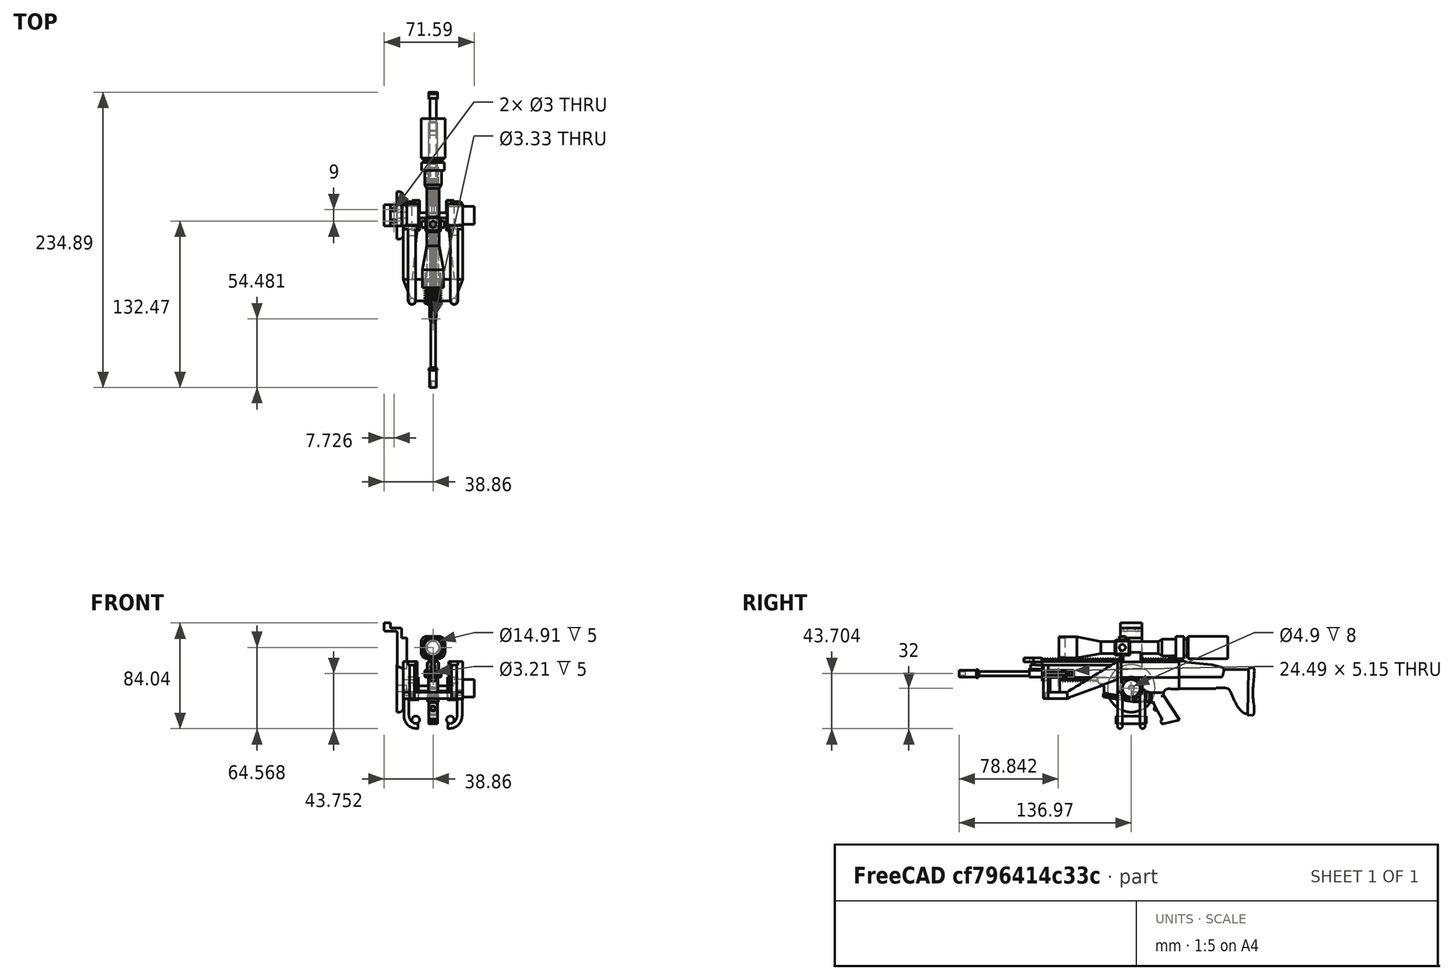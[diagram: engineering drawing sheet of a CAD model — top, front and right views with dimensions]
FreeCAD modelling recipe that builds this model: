
FCSTD DOCUMENT  (FreeCAD 1.0R39319 (Git))
Label: turretShooter
License: All rights reserved
LicenseURL: https://en.wikipedia.org/wiki/All_rights_reserved
objects: Sketcher::SketchObject×58, PartDesign::Pad×29, PartDesign::Pocket×14, PartDesign::Plane×10, PartDesign::Mirrored×8, Image::ImagePlane×4, PartDesign::Fillet×4, PartDesign::LinearPattern×3, PartDesign::Revolution×3, PartDesign::Chamfer×2, PartDesign::AdditiveLoft×1, PartDesign::AdditivePipe×1, PartDesign::MultiTransform×1, Part::Part2DObjectPython×1, PartDesign::Body×1
note: 314 computed .brp shape members not serialized (recipe doc carries the construction recipe); baked Part::Feature solids carry a one-line shape summary decoded from their .brp

FEATURE [Image::ImagePlane] The_Finals_Screenshot_2026  label="The Finals Screenshot 2026"
  Placement = pos=(0,0,0) rot=(0.57735,0.57735,0.57735;2.0944rad)
  XSize = 826.63
  YSize = 464.98
FEATURE [Image::ImagePlane] The_Finals_Screenshot_2025  label="The Finals Screenshot 2025"
  Placement = pos=(0,0,0) rot=(1,0,0;1.5708rad)
  XSize = 826.629
  YSize = 464.979
FEATURE [Image::ImagePlane] T______H___E____________F____________I_______________N______AL_________S_10_02_2025_2_09_09_pm  label="T​﻿H​E ​​​F​﻿﻿​I​﻿​﻿​N​​AL​​​S 10_02_2025 2_09_09 pm"
  Placement = pos=(0,2,83) rot=(0.57735,0.57735,0.57735;2.0944rad)
  XSize = 260.56
  YSize = 146.56
FEATURE [Image::ImagePlane] T______H___E____________F____________I_______________N______AL_________S_10_02_2025_2_07_41_pm  label="T​﻿H​E ​​​F​﻿﻿​I​﻿​﻿​N​​AL​​​S 10_02_2025 2_07_41 pm"
  Placement = pos=(0,0,92) rot=(1,0,0;1.5708rad)
  XSize = 193.32
  YSize = 108.74
FEATURE [Sketcher::SketchObject] Sketch
  ArcFitTolerance = 1e-06
  AttachmentSupport = -> [YZ_Plane]
  FullyConstrained = true
  MakeInternals = false
  MapMode = 5
  Placement = pos=(0,0,0) rot=(0.57735,0.57735,0.57735;2.0944rad)
  sketch-geometry (1):
    g0: LineSegment StartX=-70.97 StartY=87.59 StartZ=0 EndX=38.21 EndY=87.59 EndZ=0
  constraints (4):
    c: Horizontal(g0)
    c: Distance(g-1,g0) = 87.59
    c: DistanceX(g0,g0) = 109.18
    c: Distance(g0,g-2) = 70.97
FEATURE [PartDesign::Plane] DatumPlane
  AttachmentSupport = -> [Sketch,XZ_Plane]
  Length = 178.251
  MapMode = 6
  Placement = pos=(0,-70.97,87.59) rot=(0.57735,-0.57735,0.57735;2.0944rad)
  ResizeMode = 0
  Width = 92.8021
FEATURE [Sketcher::SketchObject] Sketch001
  ArcFitTolerance = 1e-06
  AttachmentSupport = -> [DatumPlane]
  FullyConstrained = true
  MakeInternals = false
  MapMode = 5
  Placement = pos=(0,-70.97,87.59) rot=(0.57735,-0.57735,0.57735;2.0944rad)
  sketch-geometry (14):
    g0: LineSegment StartX=1.18 StartY=-4.62 StartZ=0 EndX=12.07 EndY=-4.62 EndZ=0
    g1: LineSegment StartX=13.56 StartY=-3.13 StartZ=0 EndX=13.56 EndY=-2.51 EndZ=0
    g2: LineSegment StartX=13.56 StartY=-2.51 StartZ=0 EndX=15.93 EndY=-2.51 EndZ=0
    g3: LineSegment StartX=15.93 StartY=-2.51 StartZ=0 EndX=15.93 EndY=2.51 EndZ=0
    g4: LineSegment StartX=15.93 StartY=2.51 StartZ=0 EndX=13.56 EndY=2.51 EndZ=0
    g5: LineSegment StartX=13.56 StartY=2.51 StartZ=0 EndX=13.56 EndY=3.13 EndZ=0
    g6: LineSegment StartX=12.07 StartY=4.62 StartZ=0 EndX=1.18 EndY=4.62 EndZ=0
    g7: LineSegment [constr] StartX=7.37 StartY=4.62 StartZ=0 EndX=7.37 EndY=0 EndZ=0
    g8: LineSegment [constr] StartX=7.37 StartY=0 StartZ=0 EndX=7.37 EndY=-4.62 EndZ=0
    g9: LineSegment StartX=1.18 StartY=4.62 StartZ=0 EndX=1.18 EndY=-4.62 EndZ=0
    g10: ArcOfCircle CenterX=12.07 CenterY=3.13 CenterZ=0 NormalX=0 NormalY=0 NormalZ=1 AngleXU=0 Radius=1.49 StartAngle=0 EndAngle=1.5708
    g11: GeomPoint [constr] X=13.56 Y=4.62 Z=0
    g12: ArcOfCircle CenterX=12.07 CenterY=-3.13 CenterZ=0 NormalX=0 NormalY=0 NormalZ=1 AngleXU=0 Radius=1.49 StartAngle=4.71239 EndAngle=6.28319
    g13: GeomPoint [constr] X=13.56 Y=-4.62 Z=0
  constraints (38):
    c: Horizontal(g0)
    c: Vertical(g1)
    c: Coincident(g1,g2)
    c: Horizontal(g2)
    c: Coincident(g2,g3)
    c: Vertical(g3)
    c: Coincident(g3,g4)
    c: Horizontal(g4)
    c: Coincident(g4,g5)
    c: Vertical(g5)
    c: Horizontal(g6)
    c: Symmetric(g11,g6,g7)
    c: PointOnObject(g7,g-1)
    c: Vertical(g7)
    c: Coincident(g8,g7)
    c: PointOnObject(g8,g0)
    c: Vertical(g8)
    c: Equal(g8,g7)
    c: Coincident(g9,g6)
    c: Coincident(g9,g0)
    c: Vertical(g9)
    c: DistanceY(g9,g9) = 9.24
    c: DistanceX(g6,g11) = 12.38
    c: DistanceY(g3,g3) = 5.02
    c: Distance(g-1,g9) = 1.18
    c: DistanceX(g4,g4) = 2.37
    c: PointOnObject(g11,g5)
    c: PointOnObject(g11,g6)
    c: Tangent(g5,g10) = -1.5708
    c: Tangent(g6,g10) = -1.5708
    c: PointOnObject(g13,g0)
    c: PointOnObject(g13,g1)
    c: Tangent(g0,g12) = -1.5708
    c: Tangent(g1,g12) = -1.5708
    c: Equal(g12,g10)
    c: Radius(g10) = 1.49
    c: Equal(g0,g6)
    c: Equal(g1,g5)
FEATURE [PartDesign::Pad] Pad
  Direction = (0,-1,0)
  Length = 109
  Length2 = 10
  Placement = pos=(0,-70.97,87.59) rot=(0.57735,-0.57735,0.57735;2.0944rad)
  Profile = -> Sketch001
  ReferenceAxis = -> Sketch001 [N_Axis]
  Refine = true
  Reversed = true
  Suppressed = false
  Type = 0
  UpToShape = -> [Sketch]
FEATURE [Sketcher::SketchObject] Sketch002
  ArcFitTolerance = 1e-06
  AttachmentSupport = -> [YZ_Plane]
  FullyConstrained = true
  MakeInternals = false
  MapMode = 5
  Placement = pos=(0,0,0) rot=(0.57735,0.57735,0.57735;2.0944rad)
FEATURE [Sketcher::SketchObject] Sketch003
  ArcFitTolerance = 1e-06
  AttachmentSupport = -> [YZ_Plane]
  ExternalGeometry = -> [Pad]
  FullyConstrained = false
  MakeInternals = false
  MapMode = 5
  Placement = pos=(0,0,0) rot=(0.57735,0.57735,0.57735;2.0944rad)
  sketch-geometry (29):
    g0-g3: GeomPoint [constr] x4 (B-spline internal-alignment scaffolding for g4; pole/knot coordinates omitted)
    g4: BSplineCurve PolesCount=6 KnotsCount=4 Degree=3 IsPeriodic=0
    g5-g10: Circle [constr] x6 (B-spline internal-alignment scaffolding for g4; pole/knot coordinates omitted)
    g11: LineSegment StartX=-21.7658 StartY=81.0348 StartZ=0 EndX=-21.5863 EndY=76.1617 EndZ=0
    g12: LineSegment StartX=-21.5863 StartY=76.1617 StartZ=0 EndX=-22.4223 EndY=74.4999 EndZ=0
    g13: LineSegment StartX=-22.4223 StartY=74.4999 StartZ=0 EndX=-22.4223 EndY=73.2638 EndZ=0
    g14: LineSegment StartX=-22.4223 StartY=73.2638 StartZ=0 EndX=1.29753 EndY=69.2316 EndZ=0
    g15: LineSegment StartX=1.29753 StartY=69.2316 StartZ=0 EndX=1.29753 EndY=77.3277 EndZ=0
    g16: LineSegment StartX=1.29753 StartY=77.3277 StartZ=0 EndX=13.9295 EndY=77.3277 EndZ=0
    g17: LineSegment StartX=13.9295 StartY=77.3277 StartZ=0 EndX=14.8282 EndY=76.5716 EndZ=0
    g18: LineSegment StartX=14.8282 StartY=76.5716 StartZ=0 EndX=25.6744 EndY=76.5716 EndZ=0
    g19: GeomPoint [constr] X=25.6744 Y=76.5716 Z=0
    g20: GeomPoint [constr] X=27.7174 Y=79.2735 Z=0
    g21: GeomPoint [constr] X=33.2888 Y=79.6145 Z=0
    g22: BSplineCurve PolesCount=4 KnotsCount=2 Degree=3 IsPeriodic=0
    g23-g26: Circle [constr] x4 (B-spline internal-alignment scaffolding for g22; pole/knot coordinates omitted)
    g27: LineSegment StartX=33.2888 StartY=79.6145 StartZ=0 EndX=33.2888 EndY=88.77 EndZ=0
    g28: LineSegment StartX=33.2888 StartY=88.77 StartZ=0 EndX=-26.675 EndY=88.77 EndZ=0
  constraints (43):
    c: InternalAlignment(g0-g3 -> g4) x4
    c: InternalAlignment(g5,g4)
    c: Weight(g5) = 1
    c: InternalAlignment(g6,g4)
    c: Equal(g6,g5)
    c: InternalAlignment(g7,g4)
    c: Equal(g7,g5)
    c: InternalAlignment(g8,g4)
    c: Equal(g8,g5)
    c: InternalAlignment(g9,g4)
    c: Equal(g9,g5)
    c: InternalAlignment(g10,g4)
    c: Equal(g10,g5)
    c: PointOnObject(g0,g-3)
    c: Coincident(g11,g4)
    c: Coincident(g11,g12)
    c: Coincident(g12,g13)
    c: Vertical(g13)
    c: Coincident(g13,g14)
    c: Coincident(g14,g15)
    c: Vertical(g15)
    c: Coincident(g15,g16)
    c: Horizontal(g16)
    c: Coincident(g16,g17)
    c: Coincident(g17,g18)
    c: Horizontal(g18)
    c: InternalAlignment(g19,g22)
    c: PointOnObject(g20,g22)
    c: InternalAlignment(g21,g22)
    c: InternalAlignment(g23,g22)
    c: Weight(g23) = 1
    c: InternalAlignment(g24,g22)
    c: Equal(g24,g23)
    c: InternalAlignment(g25,g22)
    c: Equal(g25,g23)
    c: InternalAlignment(g26,g22)
    c: Equal(g26,g23)
    c: Coincident(g19,g18)
    c: Coincident(g27,g22)
    c: PointOnObject(g27,g-3)
    c: Vertical(g27)
    c: Coincident(g27,g28)
    c: Coincident(g28,g4)
FEATURE [PartDesign::Pad] Pad001
  BaseFeature = -> Pad
  Direction = (1,0,0)
  Length = 10
  Length2 = 10
  Midplane = true
  Offset = 1
  Placement = pos=(0,-70.97,87.59) rot=(0.57735,-0.57735,0.57735;2.0944rad)
  Profile = -> Sketch003
  ReferenceAxis = -> Sketch003 [N_Axis]
  Refine = true
  Suppressed = false
  Type = 3
  UpToFace = -> Pad [Face1]
FEATURE [PartDesign::Mirrored] Mirrored
  BaseFeature = -> Pad001
  MirrorPlane = -> YZ_Plane
  Originals = -> [Pad001]
  Placement = pos=(0,-70.97,87.59) rot=(0.57735,-0.57735,0.57735;2.0944rad)
  Refine = true
  Suppressed = false
  TransformMode = 0
FEATURE [Sketcher::SketchObject] Sketch004
  ArcFitTolerance = 1e-06
  AttachmentSupport = -> [YZ_Plane]
  ExternalGeometry = -> [Mirrored]
  FullyConstrained = false
  MakeInternals = false
  MapMode = 5
  Placement = pos=(0,0,0) rot=(0.57735,0.57735,0.57735;2.0944rad)
  sketch-geometry (17):
    g0: LineSegment StartX=16.9081 StartY=76.5716 StartZ=0 EndX=16.5743 EndY=76.3186 EndZ=0
    g1: LineSegment StartX=16.5743 StartY=76.3186 StartZ=0 EndX=16.2831 EndY=75.8195 EndZ=0
    g2: LineSegment StartX=16.2831 StartY=75.8195 StartZ=0 EndX=16.2831 EndY=68.7742 EndZ=0
    g3: LineSegment StartX=16.2831 StartY=68.7742 StartZ=0 EndX=17.4672 EndY=68.726 EndZ=0
    g4: LineSegment StartX=17.4672 StartY=68.726 StartZ=0 EndX=19.0481 EndY=65.7646 EndZ=0
    g5: LineSegment StartX=19.0481 StartY=65.7646 StartZ=0 EndX=18.1135 EndY=63.3561 EndZ=0
    g6: LineSegment StartX=18.1135 StartY=63.3561 StartZ=0 EndX=18.473 EndY=62.6731 EndZ=0
    g7: LineSegment StartX=18.473 StartY=62.6731 StartZ=0 EndX=19.6952 EndY=62.5293 EndZ=0
    g8: LineSegment StartX=19.6952 StartY=62.5293 StartZ=0 EndX=21.0612 EndY=61.9181 EndZ=0
    g9: LineSegment StartX=21.0612 StartY=61.9181 StartZ=0 EndX=24.3711 EndY=55.6421 EndZ=0
    g10: LineSegment StartX=24.3711 StartY=55.6421 StartZ=0 EndX=23.5443 EndY=53.665 EndZ=0
    g11: LineSegment StartX=23.5443 StartY=53.665 StartZ=0 EndX=24.5508 EndY=51.7957 EndZ=0
    g12: LineSegment StartX=24.5508 StartY=51.7957 StartZ=0 EndX=37.0608 EndY=54.4199 EndZ=0
    g13: LineSegment StartX=37.0608 StartY=54.4199 StartZ=0 EndX=38.3549 EndY=55.1388 EndZ=0
    g14: LineSegment StartX=38.3549 StartY=55.1388 StartZ=0 EndX=25.6744 EndY=74.3298 EndZ=0
    g15: LineSegment StartX=25.6744 StartY=74.3298 StartZ=0 EndX=25.6744 EndY=76.5716 EndZ=0
    g16: LineSegment StartX=16.9081 StartY=76.5716 StartZ=0 EndX=25.6744 EndY=76.5716 EndZ=0
  constraints (21):
    c: PointOnObject(g0,g-3)
    c: Coincident(g0,g1)
    c: Coincident(g1,g2)
    c: Vertical(g2)
    c: Coincident(g2,g3)
    c: Coincident(g3,g4)
    c: Coincident(g4,g5)
    c: Coincident(g5,g6)
    c: Coincident(g6,g7)
    c: Coincident(g7,g8)
    c: Coincident(g8,g9)
    c: Coincident(g9,g10)
    c: Coincident(g10,g11)
    c: Coincident(g11,g12)
    c: Coincident(g12,g13)
    c: Coincident(g13,g14)
    c: Coincident(g14,g15)
    c: Coincident(g15,g-3)
    c: Vertical(g15)
    c: Coincident(g16,g0)
    c: Coincident(g16,g15)
FEATURE [PartDesign::Pad] Pad002
  BaseFeature = -> Mirrored
  Direction = (1,0,0)
  Length = 7
  Length2 = 10
  Midplane = true
  Placement = pos=(0,-70.97,87.59) rot=(0.57735,-0.57735,0.57735;2.0944rad)
  Profile = -> Sketch004
  ReferenceAxis = -> Sketch004 [N_Axis]
  Refine = true
  Suppressed = false
  Type = 0
FEATURE [Sketcher::SketchObject] Sketch005
  ArcFitTolerance = 1e-06
  AttachmentSupport = -> [Pad002]
  ExternalGeometry = -> [Pad002]
  FullyConstrained = false
  MakeInternals = false
  MapMode = 5
  Placement = pos=(3.5,-70.97,87.59) rot=(0.707107,0,0.707107;3.14159rad)
  sketch-geometry (4):
    g0: LineSegment StartX=-25.6719 StartY=-92.0312 StartZ=0 EndX=-21.8254 EndY=-90.0181 EndZ=0
    g1: LineSegment StartX=-25.6719 StartY=-92.0312 StartZ=0 EndX=-26.772 EndY=-88.7379 EndZ=0
    g2: LineSegment StartX=-26.772 StartY=-88.7379 StartZ=0 EndX=-23.2386 EndY=-88.3381 EndZ=0
    g3: LineSegment StartX=-23.2386 StartY=-88.3381 StartZ=0 EndX=-21.8254 EndY=-90.0181 EndZ=0
  constraints (6):
    c: Coincident(g-9,g0)
    c: Coincident(g0,g-4)
    c: Coincident(g0,g1)
    c: Coincident(g1,g2)
    c: Coincident(g2,g3)
    c: Coincident(g3,g0)
FEATURE [PartDesign::Pocket] Pocket
  BaseFeature = -> Pad002
  Direction = (-1,0,2e-16)
  Length = 2
  Length2 = 5
  Placement = pos=(0,-70.97,87.59) rot=(0.57735,-0.57735,0.57735;2.0944rad)
  Profile = -> Sketch005
  ReferenceAxis = -> Sketch005 [N_Axis]
  Refine = true
  Suppressed = false
  Type = 0
FEATURE [PartDesign::Mirrored] Mirrored001
  BaseFeature = -> Pocket
  MirrorPlane = -> YZ_Plane
  Originals = -> [Pocket]
  Placement = pos=(0,-70.97,87.59) rot=(0.57735,-0.57735,0.57735;2.0944rad)
  Refine = true
  Suppressed = false
  TransformMode = 0
FEATURE [PartDesign::Fillet] Fillet
  Base = -> Mirrored001 [Edge88,Edge87,Edge86,Edge85,Edge84,Edge100,Edge101,Edge102,Edge99,Edge98]
  BaseFeature = -> Mirrored001
  Placement = pos=(0,-70.97,87.59) rot=(0.57735,-0.57735,0.57735;2.0944rad)
  Radius = 1
  Refine = true
  SupportTransform = false
  Suppressed = false
  UseAllEdges = false
FEATURE [PartDesign::Fillet] Fillet001
  Base = -> Fillet [Edge5,Edge7,Edge28,Edge33]
  BaseFeature = -> Fillet
  Placement = pos=(0,-70.97,87.59) rot=(0.57735,-0.57735,0.57735;2.0944rad)
  Radius = 2
  Refine = true
  SupportTransform = false
  Suppressed = false
  UseAllEdges = false
FEATURE [PartDesign::Fillet] Fillet002
  Base = -> Fillet001 [Edge139,Edge162,Edge136,Edge161]
  BaseFeature = -> Fillet001
  Placement = pos=(0,-70.97,87.59) rot=(0.57735,-0.57735,0.57735;2.0944rad)
  Radius = 0.5
  Refine = true
  SupportTransform = false
  Suppressed = false
  UseAllEdges = false
FEATURE [PartDesign::Pad] Pad003
  BaseFeature = -> Fillet002
  Direction = (1e-16,1,0)
  Length = 10
  Length2 = 10
  Placement = pos=(0,-70.97,87.59) rot=(0.57735,-0.57735,0.57735;2.0944rad)
  Profile = -> Fillet002 [Face47]
  Refine = true
  Suppressed = false
  Type = 3
  UpToFace = -> Fillet002 [Face59]
FEATURE [Sketcher::SketchObject] Sketch006
  ArcFitTolerance = 1e-06
  AttachmentSupport = -> [YZ_Plane]
  ExternalGeometry = -> [Pad003]
  FullyConstrained = false
  MakeInternals = false
  MapMode = 5
  Placement = pos=(0,0,0) rot=(0.57735,0.57735,0.57735;2.0944rad)
  sketch-geometry (35):
    g0: LineSegment StartX=1.64111 StartY=70.8438 StartZ=0 EndX=2.72621 EndY=70.1138 EndZ=0
    g1: LineSegment StartX=2.72621 StartY=70.1138 StartZ=0 EndX=13.0839 EndY=69.8573 EndZ=0
    g2: LineSegment StartX=13.0839 StartY=69.8573 StartZ=0 EndX=13.6758 EndY=70.1533 EndZ=0
    g3: LineSegment StartX=13.6758 StartY=70.1533 StartZ=0 EndX=14.2084 EndY=70.5873 EndZ=0
    g4: LineSegment StartX=14.2084 StartY=70.5873 StartZ=0 EndX=14.5241 EndY=71.1397 EndZ=0
    g5: LineSegment StartX=14.5241 StartY=71.1397 StartZ=0 EndX=14.5241 EndY=76.8274 EndZ=0
    g6: LineSegment StartX=14.5241 StartY=76.8274 StartZ=0 EndX=13.9295 EndY=77.3277 EndZ=0
    g7: LineSegment StartX=2.3119 StartY=77.3277 StartZ=0 EndX=1.8384 EndY=76.9203 EndZ=0
    g8: LineSegment StartX=1.8384 StartY=76.9203 StartZ=0 EndX=1.64111 EndY=76.6441 EndZ=0
    g9: LineSegment StartX=1.64111 StartY=76.6441 StartZ=0 EndX=1.64111 EndY=70.8438 EndZ=0
    g10: LineSegment StartX=1.29754 StartY=69.2316 StartZ=0 EndX=16.2831 EndY=69.2316 EndZ=0
    g11: LineSegment StartX=16.2831 StartY=69.2316 StartZ=0 EndX=18.1597 EndY=78.374 EndZ=0
    g12: LineSegment StartX=18.1597 StartY=78.374 StartZ=0 EndX=0.618146 EndY=78.374 EndZ=0
    g13: LineSegment StartX=0.618146 StartY=78.374 StartZ=0 EndX=1.29754 EndY=69.2316 EndZ=0
    g14: LineSegment StartX=13.9295 StartY=77.3277 StartZ=0 EndX=11.92 EndY=77.3277 EndZ=0
    g15: LineSegment StartX=11.92 StartY=77.3277 StartZ=0 EndX=11.92 EndY=72.0294 EndZ=0
    g16-g19: Circle [constr] x4 (B-spline internal-alignment scaffolding for g20; pole/knot coordinates omitted)
    g20: BSplineCurve PolesCount=4 KnotsCount=2 Degree=3 IsPeriodic=0
    g21: GeomPoint [constr] X=11.92 Y=72.0294 Z=0
    g22: GeomPoint [constr] X=9.76933 Y=70.1931 Z=0
    g23-g26: GeomPoint [constr] x4 (B-spline internal-alignment scaffolding for g27; pole/knot coordinates omitted)
    g27: BSplineCurve PolesCount=6 KnotsCount=4 Degree=3 IsPeriodic=0
    g28-g33: Circle [constr] x6 (B-spline internal-alignment scaffolding for g27; pole/knot coordinates omitted)
    g34: LineSegment StartX=7.6135 StartY=77.3277 StartZ=0 EndX=2.3119 EndY=77.3277 EndZ=0
  constraints (52):
    c: Coincident(g0,g1)
    c: Coincident(g1,g2)
    c: Coincident(g2,g3)
    c: Coincident(g3,g4)
    c: Coincident(g4,g5)
    c: PointOnObject(g5,g-6)
    c: Vertical(g5)
    c: Coincident(g5,g6)
    c: Coincident(g6,g-6)
    c: PointOnObject(g7,g-4)
    c: Coincident(g7,g8)
    c: Coincident(g8,g9)
    c: Vertical(g9)
    c: Coincident(g0,g9)
    c: Coincident(g-3,g10)
    c: PointOnObject(g10,g-7)
    c: Horizontal(g10)
    c: Coincident(g10,g11)
    c: Coincident(g11,g12)
    c: Horizontal(g12)
    c: Coincident(g12,g13)
    c: Coincident(g13,g10)
    c: Coincident(g6,g14)
    c: PointOnObject(g14,g-4)
    c: Coincident(g14,g15)
    c: Vertical(g15)
    c: Weight(g16) = 1
    c: Equal(g16,g17)
    c: Equal(g16,g18)
    c: Equal(g16,g19)
    c: InternalAlignment(g16-g19 -> g20) x4
    c: InternalAlignment(g21,g20)
    c: InternalAlignment(g22,g20)
    c: Coincident(g16,g15)
    c: PointOnObject(g19,g17)
    c: InternalAlignment(g23-g26 -> g27) x4
    c: InternalAlignment(g28,g27)
    c: Weight(g28) = 1
    c: InternalAlignment(g29,g27)
    c: Equal(g29,g28)
    c: InternalAlignment(g30,g27)
    c: Equal(g30,g28)
    c: InternalAlignment(g31,g27)
    c: Equal(g31,g28)
    c: InternalAlignment(g32,g27)
    c: Equal(g32,g28)
    c: InternalAlignment(g33,g27)
    c: Equal(g33,g28)
    c: Coincident(g23,g20)
    c: Symmetric(g-4,g-4,g26)
    c: Coincident(g34,g27)
    c: Coincident(g34,g7)
FEATURE [PartDesign::Pad] Pad004
  BaseFeature = -> Pad003
  Direction = (1,0,0)
  Length = 2
  Length2 = 10
  Midplane = true
  Placement = pos=(0,-70.97,87.59) rot=(0.57735,-0.57735,0.57735;2.0944rad)
  Profile = -> Sketch006
  ReferenceAxis = -> Sketch006 [N_Axis]
  Refine = true
  Suppressed = false
  Type = 0
FEATURE [Sketcher::SketchObject] Sketch008
  ArcFitTolerance = 1e-06
  AttachmentSupport = -> [Pad004]
  FullyConstrained = false
  MakeInternals = false
  MapMode = 5
  Placement = pos=(0,-70.97,87.59) rot=(0.57735,-0.57735,0.57735;2.0944rad)
  sketch-geometry (1):
    g0: Circle CenterX=4.16197 CenterY=0 CenterZ=0 NormalX=0 NormalY=0 NormalZ=1 AngleXU=0 Radius=2.67231
  constraints (1):
    c: PointOnObject(g0,g-1)
FEATURE [PartDesign::Pad] Pad006
  BaseFeature = -> Pad004
  Direction = (0,-1,0)
  Length = 10
  Length2 = 10
  Placement = pos=(0,-70.97,87.59) rot=(0.57735,-0.57735,0.57735;2.0944rad)
  Profile = -> Sketch008
  ReferenceAxis = -> Sketch008 [N_Axis]
  Refine = true
  Suppressed = false
  Type = 0
FEATURE [Sketcher::SketchObject] Sketch009
  ArcFitTolerance = 1e-06
  AttachmentSupport = -> [Pad006]
  ExternalGeometry = -> [Pad006]
  FullyConstrained = false
  MakeInternals = false
  MapMode = 5
  Placement = pos=(0,-80.97,87.59) rot=(0.57735,-0.57735,0.57735;2.0944rad)
  sketch-geometry (1):
    g0: Circle CenterX=4.16197 CenterY=0 CenterZ=0 NormalX=0 NormalY=0 NormalZ=1 AngleXU=0 Radius=1.8522
  constraints (1):
    c: Coincident(g0,g-3)
FEATURE [PartDesign::Pad] Pad007
  BaseFeature = -> Pad006
  Direction = (0,-1,0)
  Length = 40
  Length2 = 10
  Placement = pos=(0,-70.97,87.59) rot=(0.57735,-0.57735,0.57735;2.0944rad)
  Profile = -> Sketch009
  ReferenceAxis = -> Sketch009 [N_Axis]
  Refine = true
  Suppressed = false
  Type = 0
FEATURE [Sketcher::SketchObject] Sketch010
  ArcFitTolerance = 1e-06
  AttachmentSupport = -> [Pad007]
  ExternalGeometry = -> [Pad007]
  FullyConstrained = false
  MakeInternals = false
  MapMode = 5
  Placement = pos=(0,1.29753,87.59) rot=(0.57735,0.57735,0.57735;4.18879rad)
  sketch-geometry (4):
    g0: LineSegment StartX=-15.2831 StartY=3.62 StartZ=0 EndX=-16.9708 EndY=4.36603 EndZ=0
    g1: LineSegment StartX=-16.9708 StartY=4.36603 StartZ=0 EndX=-18.3584 EndY=4.36603 EndZ=0
    g2: LineSegment StartX=-18.3584 StartY=4.36603 StartZ=0 EndX=-18.3584 EndY=3.62 EndZ=0
    g3: LineSegment StartX=-18.3584 StartY=3.62 StartZ=0 EndX=-15.2831 EndY=3.62 EndZ=0
  constraints (8):
    c: Coincident(g0,g1)
    c: Horizontal(g1)
    c: Coincident(g1,g2)
    c: Coincident(g2,g-4)
    c: Coincident(g2,g3)
    c: Coincident(g3,g0)
    c: Vertical(g2)
    c: PointOnObject(g0,g-4)
FEATURE [PartDesign::Pad] Pad008
  BaseFeature = -> Pad007
  Direction = (-7e-16,0.985857,-0.167587)
  Length = 25
  Length2 = 10
  Placement = pos=(0,-70.97,87.59) rot=(0.57735,-0.57735,0.57735;2.0944rad)
  Profile = -> Sketch010
  ReferenceAxis = -> Pad007 [Edge158]
  Refine = true
  Reversed = true
  Suppressed = false
  Type = 3
  UpToFace = -> Pad007 [Face69]
FEATURE [PartDesign::Pocket] Pocket001
  BaseFeature = -> Pad008
  Direction = (1,0,-6.3e-15)
  Length = 5
  Length2 = 5
  Placement = pos=(0,-70.97,87.59) rot=(0.57735,-0.57735,0.57735;2.0944rad)
  Profile = -> Pad008 [Face87]
  Refine = true
  Suppressed = false
  Type = 0
FEATURE [Sketcher::SketchObject] Sketch011
  ArcFitTolerance = 1e-06
  AttachmentSupport = -> [Pocket001]
  ExternalGeometry = -> [Pocket001]
  FullyConstrained = false
  MakeInternals = false
  MapMode = 5
  Placement = pos=(3.62,-70.97,87.59) rot=(0.707107,0,0.707107;3.14159rad)
  sketch-geometry (4):
    g0: LineSegment StartX=-18.3584 StartY=-72.2675 StartZ=0 EndX=-18.3584 EndY=-73.1783 EndZ=0
    g1: LineSegment StartX=-18.3584 StartY=-73.1783 StartZ=0 EndX=-16.9935 EndY=-73.1783 EndZ=0
    g2: LineSegment StartX=-16.9935 StartY=-73.1783 StartZ=0 EndX=-15.2831 EndY=-72.2675 EndZ=0
    g3: LineSegment StartX=-15.2831 StartY=-72.2675 StartZ=0 EndX=-18.3584 EndY=-72.2675 EndZ=0
  constraints (8):
    c: Coincident(g-4,g0)
    c: Vertical(g0)
    c: Coincident(g0,g1)
    c: Horizontal(g1)
    c: Coincident(g1,g2)
    c: Coincident(g2,g-5)
    c: Coincident(g2,g3)
    c: Coincident(g3,g0)
FEATURE [PartDesign::Pad] Pad009
  BaseFeature = -> Pocket001
  Direction = (1,1.3e-15,1.8e-15)
  Length = 4
  Length2 = 3
  Placement = pos=(0,-70.97,87.59) rot=(0.57735,-0.57735,0.57735;2.0944rad)
  Profile = -> Sketch011
  ReferenceAxis = -> Sketch011 [N_Axis]
  Refine = true
  Reversed = true
  Suppressed = false
  Type = 4
FEATURE [PartDesign::Pocket] Pocket002
  BaseFeature = -> Pad009
  Direction = (-1.7e-15,1,2e-16)
  Length = 5
  Length2 = 5
  Placement = pos=(0,-70.97,87.59) rot=(0.57735,-0.57735,0.57735;2.0944rad)
  Profile = -> Pad009 [Face94]
  Refine = true
  Suppressed = false
  Type = 0
FEATURE [PartDesign::Mirrored] Mirrored002
  BaseFeature = -> Pocket002
  MirrorPlane = -> YZ_Plane
  Originals = -> [Pad008,Pocket001,Pad009,Pocket002]
  Placement = pos=(0,-70.97,87.59) rot=(0.57735,-0.57735,0.57735;2.0944rad)
  Refine = true
  Suppressed = false
  TransformMode = 0
FEATURE [Sketcher::SketchObject] Sketch012
  ArcFitTolerance = 1e-06
  AttachmentSupport = -> [Mirrored002]
  FullyConstrained = false
  MakeInternals = false
  MapMode = 5
  Placement = pos=(0,-70.97,87.59) rot=(0.57735,-0.57735,0.57735;2.0944rad)
  sketch-geometry (1):
    g0: Circle CenterX=9.39539 CenterY=0 CenterZ=0 NormalX=0 NormalY=0 NormalZ=1 AngleXU=0 Radius=1.79676
  constraints (1):
    c: PointOnObject(g0,g-1)
FEATURE [PartDesign::Pad] Pad010
  BaseFeature = -> Mirrored002
  Direction = (2.7e-15,-1,0)
  Length = 9
  Length2 = 10
  Placement = pos=(0,-70.97,87.59) rot=(0.57735,-0.57735,0.57735;2.0944rad)
  Profile = -> Sketch012
  ReferenceAxis = -> Sketch012 [N_Axis]
  Refine = true
  Suppressed = false
  Type = 0
FEATURE [Sketcher::SketchObject] Sketch013
  ArcFitTolerance = 1e-06
  AttachmentSupport = -> [Pad010]
  FullyConstrained = false
  MakeInternals = false
  MapMode = 5
  Placement = pos=(0,-70.97,87.59) rot=(0.57735,-0.57735,0.57735;2.0944rad)
  sketch-geometry (1):
    g0: Circle CenterX=7.61512 CenterY=0 CenterZ=0 NormalX=0 NormalY=0 NormalZ=1 AngleXU=0 Radius=0.743488
  constraints (1):
    c: PointOnObject(g0,g-1)
FEATURE [PartDesign::Pad] Pad011
  BaseFeature = -> Pad010
  Direction = (3.1e-15,-1,0)
  Length = 10
  Length2 = 10
  Placement = pos=(0,-70.97,87.59) rot=(0.57735,-0.57735,0.57735;2.0944rad)
  Profile = -> Sketch013
  ReferenceAxis = -> Sketch013 [N_Axis]
  Refine = true
  Suppressed = false
  Type = 0
FEATURE [Sketcher::SketchObject] Sketch014
  ArcFitTolerance = 1e-06
  AttachmentSupport = -> [Pad011]
  FullyConstrained = false
  MakeInternals = false
  MapMode = 5
  Placement = pos=(0,-70.97,87.59) rot=(0.57735,-0.57735,0.57735;2.0944rad)
  sketch-geometry (5):
    g0: LineSegment StartX=13.5625 StartY=-1.01117 StartZ=0 EndX=13.5625 EndY=1.01117 EndZ=0
    g1: LineSegment StartX=13.5625 StartY=1.01117 StartZ=0 EndX=10.7154 EndY=1.01117 EndZ=0
    g2: LineSegment StartX=10.7154 StartY=1.01117 StartZ=0 EndX=10.7154 EndY=-1.01117 EndZ=0
    g3: LineSegment StartX=10.7154 StartY=-1.01117 StartZ=0 EndX=13.5625 EndY=-1.01117 EndZ=0
    g4: GeomPoint [constr] X=12.139 Y=0 Z=0
  constraints (10):
    c: Coincident(g0,g1)
    c: Coincident(g1,g2)
    c: Coincident(g2,g3)
    c: Coincident(g3,g0)
    c: Vertical(g0)
    c: Vertical(g2)
    c: Horizontal(g1)
    c: Horizontal(g3)
    c: Symmetric(g2,g0,g4)
    c: PointOnObject(g4,g-1)
FEATURE [PartDesign::Pad] Pad012
  BaseFeature = -> Pad011
  Direction = (3.6e-15,-1,0)
  Length = 6
  Length2 = 10
  Placement = pos=(0,-70.97,87.59) rot=(0.57735,-0.57735,0.57735;2.0944rad)
  Profile = -> Sketch014
  ReferenceAxis = -> Sketch014 [N_Axis]
  Refine = true
  Suppressed = false
  Type = 0
FEATURE [Sketcher::SketchObject] Sketch015
  ArcFitTolerance = 1e-06
  AttachmentSupport = -> [Pad012]
  ExternalGeometry = -> [Pad012]
  FullyConstrained = false
  MakeInternals = false
  MapMode = 5
  Placement = pos=(0,-70.97,101.153) rot=(0,0,1;3.14159rad)
  sketch-geometry (26):
    g0: LineSegment StartX=0 StartY=0 StartZ=0 EndX=-1.03961 EndY=4.2e-15 EndZ=0
    g1: LineSegment StartX=-1.03961 StartY=4.2e-15 StartZ=0 EndX=-1.03961 EndY=6.84548 EndZ=0
    g2-g5: GeomPoint [constr] x4 (B-spline internal-alignment scaffolding for g6; pole/knot coordinates omitted)
    g6: BSplineCurve PolesCount=6 KnotsCount=4 Degree=3 IsPeriodic=0
    g7-g12: Circle [constr] x6 (B-spline internal-alignment scaffolding for g6; pole/knot coordinates omitted)
    g13: LineSegment StartX=0 StartY=0 StartZ=0 EndX=1.03961 EndY=4.2e-15 EndZ=0
    g14: LineSegment StartX=1.03961 StartY=4.2e-15 StartZ=0 EndX=1.03961 EndY=6.84548 EndZ=0
    g15-g18: GeomPoint [constr] x4 (B-spline internal-alignment scaffolding for g19; pole/knot coordinates omitted)
    g19: BSplineCurve PolesCount=6 KnotsCount=4 Degree=3 IsPeriodic=0
    g20-g25: Circle [constr] x6 (B-spline internal-alignment scaffolding for g19; pole/knot coordinates omitted)
  constraints (35):
    c: Coincident(g-1,g0)
    c: PointOnObject(g0,g-3)
    c: Coincident(g0,g1)
    c: Vertical(g1)
    c: InternalAlignment(g2-g5 -> g6) x4
    c: InternalAlignment(g7,g6)
    c: Weight(g7) = 1
    c: InternalAlignment(g8,g6)
    c: Equal(g8,g7)
    c: InternalAlignment(g9,g6)
    c: Equal(g9,g7)
    c: InternalAlignment(g10,g6)
    c: Equal(g10,g7)
    c: InternalAlignment(g11,g6)
    c: Equal(g11,g7)
    c: InternalAlignment(g12,g6)
    c: Equal(g12,g7)
    c: Coincident(g2,g1)
    c: PointOnObject(g5,g-2)
    c: Coincident(g13,g14)
    c: Vertical(g14)
    c: InternalAlignment(g15-g18 -> g19) x4
    c: InternalAlignment(g20,g19)
    c: Weight(g20) = 1
    c: InternalAlignment(g21,g19)
    c: Equal(g21,g20)
    c: InternalAlignment(g22,g19)
    c: Equal(g22,g20)
    c: InternalAlignment(g23,g19)
    c: Equal(g23,g20)
    c: InternalAlignment(g24,g19)
    c: Equal(g24,g20)
    c: InternalAlignment(g25,g19)
    c: Equal(g25,g20)
    c: Coincident(g15,g14)
FEATURE [PartDesign::Pad] Pad013
  BaseFeature = -> Pad012
  Direction = (0,0,1)
  Length = 3
  Length2 = 10
  Placement = pos=(0,-70.97,87.59) rot=(0.57735,-0.57735,0.57735;2.0944rad)
  Profile = -> Sketch015
  ReferenceAxis = -> Sketch015 [N_Axis]
  Refine = true
  Suppressed = false
  Type = 0
FEATURE [Sketcher::SketchObject] Sketch016
  ArcFitTolerance = 1e-06
  AttachmentSupport = -> [Pad013]
  ExternalGeometry = -> [Pad013]
  FullyConstrained = false
  MakeInternals = false
  MapMode = 5
  Placement = pos=(0,38.03,87.59) rot=(0.57735,0.57735,0.57735;4.18879rad)
  sketch-geometry (14):
    g0: LineSegment StartX=15.2045 StartY=-2.51 StartZ=0 EndX=14.973 EndY=-2.11717 EndZ=0
    g1: LineSegment StartX=14.973 StartY=-2.11717 StartZ=0 EndX=14.4883 EndY=-2.51188 EndZ=0
    g2: LineSegment StartX=14.4883 StartY=-2.51188 StartZ=0 EndX=15.2045 EndY=-2.51 EndZ=0
    g3: LineSegment StartX=15.7121 StartY=-2.51 StartZ=0 EndX=15.93 EndY=-2.11035 EndZ=0
    g4: LineSegment StartX=15.93 StartY=-2.11035 StartZ=0 EndX=16.3253 EndY=-2.56622 EndZ=0
    g5: LineSegment StartX=16.3253 StartY=-2.56622 StartZ=0 EndX=15.7121 EndY=-2.80869 EndZ=0
    g6: LineSegment StartX=15.7121 StartY=-2.80869 StartZ=0 EndX=15.7121 EndY=-2.51 EndZ=0
    g7: LineSegment StartX=15.2045 StartY=2.51 StartZ=0 EndX=14.973 EndY=2.11717 EndZ=0
    g8: LineSegment StartX=14.973 StartY=2.11717 StartZ=0 EndX=14.4883 EndY=2.51188 EndZ=0
    g9: LineSegment StartX=14.4883 StartY=2.51188 StartZ=0 EndX=15.2045 EndY=2.51 EndZ=0
    g10: LineSegment StartX=15.7121 StartY=2.51 StartZ=0 EndX=15.93 EndY=2.11035 EndZ=0
    g11: LineSegment StartX=15.93 StartY=2.11035 StartZ=0 EndX=16.3253 EndY=2.56622 EndZ=0
    g12: LineSegment StartX=16.3253 StartY=2.56622 StartZ=0 EndX=15.7121 EndY=2.80869 EndZ=0
    g13: LineSegment StartX=15.7121 StartY=2.80869 StartZ=0 EndX=15.7121 EndY=2.51 EndZ=0
  constraints (19):
    c: PointOnObject(g0,g-5)
    c: Coincident(g0,g1)
    c: Coincident(g1,g2)
    c: Coincident(g2,g0)
    c: PointOnObject(g3,g-5)
    c: PointOnObject(g3,g-4)
    c: Coincident(g3,g4)
    c: Coincident(g4,g5)
    c: Coincident(g5,g6)
    c: Coincident(g6,g3)
    c: Vertical(g6)
    c: Coincident(g7,g8)
    c: Coincident(g8,g9)
    c: Coincident(g9,g7)
    c: Coincident(g10,g11)
    c: Coincident(g11,g12)
    c: Coincident(g12,g13)
    c: Coincident(g13,g10)
    c: Vertical(g13)
FEATURE [PartDesign::Pocket] Pocket003
  BaseFeature = -> Pad013
  Direction = (4.3e-15,-1,-1e-15)
  Length = 0
  Length2 = 5
  Placement = pos=(0,-70.97,87.59) rot=(0.57735,-0.57735,0.57735;2.0944rad)
  Profile = -> Sketch016
  ReferenceAxis = -> Sketch016 [N_Axis]
  Refine = true
  Suppressed = false
  Type = 3
  UpToFace = -> Pad013 [Face70]
FEATURE [Sketcher::SketchObject] Sketch017
  ArcFitTolerance = 1e-06
  AttachmentSupport = -> [Pocket003]
  ExternalGeometry = -> [Pocket003]
  FullyConstrained = true
  MakeInternals = false
  MapMode = 5
  Placement = pos=(4.62,-70.97,87.59) rot=(0.707107,0,0.707107;3.14159rad)
  sketch-geometry (4):
    g0: LineSegment StartX=15.93 StartY=-1 StartZ=0 EndX=15.23 EndY=-1 EndZ=0
    g1: LineSegment StartX=15.23 StartY=-1 StartZ=0 EndX=15.23 EndY=-2 EndZ=0
    g2: LineSegment StartX=15.23 StartY=-2 StartZ=0 EndX=15.93 EndY=-2 EndZ=0
    g3: LineSegment StartX=15.93 StartY=-2 StartZ=0 EndX=15.93 EndY=-1 EndZ=0
  constraints (12):
    c: Coincident(g0,g1)
    c: Coincident(g1,g2)
    c: Coincident(g2,g3)
    c: Coincident(g3,g0)
    c: Horizontal(g0)
    c: Horizontal(g2)
    c: Vertical(g1)
    c: Vertical(g3)
    c: PointOnObject(g0,g-3)
    c: DistanceY(g3,g3) = 1
    c: Distance(g0,g-1) = 1
    c: DistanceX(g0,g0) = 0.7
FEATURE [PartDesign::Pocket] Pocket004
  BaseFeature = -> Pocket003
  Direction = (-1,-3.7e-15,-4.9e-15)
  Length = 5
  Length2 = 5
  Placement = pos=(0,-70.97,87.59) rot=(0.57735,-0.57735,0.57735;2.0944rad)
  Profile = -> Sketch017
  ReferenceAxis = -> Sketch017 [N_Axis]
  Refine = true
  Suppressed = false
  Type = 1
FEATURE [PartDesign::LinearPattern] LinearPattern
  BaseFeature = -> Pocket004
  Direction = -> Y_Axis
  Length = 98
  Mode = 1
  Occurrences = 50
  Offset = 2
  Originals = -> [Pocket004]
  Placement = pos=(0,-70.97,87.59) rot=(0.57735,-0.57735,0.57735;2.0944rad)
  Refine = true
  Suppressed = false
  TransformMode = 0
FEATURE [Sketcher::SketchObject] Sketch018
  ArcFitTolerance = 1e-06
  AttachmentSupport = -> [LinearPattern]
  FullyConstrained = false
  MakeInternals = false
  MapMode = 5
  Placement = pos=(0,-70.97,104.153) rot=(0,0,1;3.14159rad)
  sketch-geometry (5):
    g0: Circle CenterX=0 CenterY=11.5186 CenterZ=0 NormalX=0 NormalY=0 NormalZ=1 AngleXU=0 Radius=1.66471
    g1: LineSegment StartX=-1.21028 StartY=0 StartZ=0 EndX=1.19759 EndY=0 EndZ=0
    g2: LineSegment StartX=1.19759 StartY=0 StartZ=0 EndX=1.19759 EndY=0.298211 EndZ=0
    g3: LineSegment StartX=1.19759 StartY=0.298211 StartZ=0 EndX=-1.21028 EndY=0.298211 EndZ=0
    g4: LineSegment StartX=-1.21028 StartY=0.298211 StartZ=0 EndX=-1.21028 EndY=0 EndZ=0
  constraints (10):
    c: PointOnObject(g0,g-2)
    c: Coincident(g1,g2)
    c: Coincident(g2,g3)
    c: Coincident(g3,g4)
    c: Coincident(g4,g1)
    c: Horizontal(g1)
    c: Horizontal(g3)
    c: Vertical(g2)
    c: Vertical(g4)
    c: PointOnObject(g1,g-1)
FEATURE [PartDesign::Pocket] Pocket005
  BaseFeature = -> LinearPattern
  Direction = (0,0,-1)
  Length = 5
  Length2 = 5
  Placement = pos=(0,-70.97,87.59) rot=(0.57735,-0.57735,0.57735;2.0944rad)
  Profile = -> Sketch018
  ReferenceAxis = -> Sketch018 [N_Axis]
  Refine = true
  Suppressed = false
  Type = 2
FEATURE [Sketcher::SketchObject] Sketch019
  ArcFitTolerance = 1e-06
  AttachmentSupport = -> [Pocket005]
  ExternalGeometry = -> [Pocket005]
  FullyConstrained = false
  MakeInternals = false
  MapMode = 5
  Placement = pos=(0,-120.97,87.59) rot=(0.57735,-0.57735,0.57735;2.0944rad)
  sketch-geometry (1):
    g0: Circle CenterX=4.16197 CenterY=4.3e-15 CenterZ=0 NormalX=0 NormalY=0 NormalZ=1 AngleXU=0 Radius=2.60528
  constraints (1):
    c: Coincident(g0,g-3)
FEATURE [PartDesign::Pad] Pad014
  BaseFeature = -> Pocket005
  Direction = (5.3e-15,-1,-1.3e-15)
  Length = 16
  Length2 = 10
  Placement = pos=(0,-70.97,87.59) rot=(0.57735,-0.57735,0.57735;2.0944rad)
  Profile = -> Sketch019
  ReferenceAxis = -> Sketch019 [N_Axis]
  Refine = true
  Suppressed = false
  Type = 0
FEATURE [Sketcher::SketchObject] Sketch020
  ArcFitTolerance = 1e-06
  AttachmentSupport = -> [YZ_Plane]
  FullyConstrained = false
  MakeInternals = false
  MapMode = 5
  Placement = pos=(0,0,0) rot=(0.57735,0.57735,0.57735;2.0944rad)
  sketch-geometry (4):
    g0: LineSegment StartX=-123.209 StartY=93.8586 StartZ=0 EndX=-122.134 EndY=93.8586 EndZ=0
    g1: LineSegment StartX=-122.134 StartY=93.8586 StartZ=0 EndX=-122.134 EndY=95.0143 EndZ=0
    g2: LineSegment StartX=-122.134 StartY=95.0143 StartZ=0 EndX=-123.209 EndY=95.0143 EndZ=0
    g3: LineSegment StartX=-123.209 StartY=95.0143 StartZ=0 EndX=-123.209 EndY=93.8586 EndZ=0
  constraints (8):
    c: Coincident(g0,g1)
    c: Coincident(g1,g2)
    c: Coincident(g2,g3)
    c: Coincident(g3,g0)
    c: Horizontal(g0)
    c: Horizontal(g2)
    c: Vertical(g1)
    c: Vertical(g3)
FEATURE [PartDesign::Revolution] Revolution
  Angle = 360
  Angle2 = 60
  Axis = (5.7e-15,-1,-1.6e-15)
  Base = (3.753e-13,-136.97,91.752)
  BaseFeature = -> Pad014
  Placement = pos=(0,-70.97,87.59) rot=(0.57735,-0.57735,0.57735;2.0944rad)
  Profile = -> Sketch020
  ReferenceAxis = -> Pad014 [Edge1248]
  Refine = true
  Suppressed = false
  Type = 0
FEATURE [Sketcher::SketchObject] Sketch021
  ArcFitTolerance = 1e-06
  AttachmentSupport = -> [Revolution]
  ExternalGeometry = -> [Revolution]
  FullyConstrained = true
  MakeInternals = false
  MapMode = 5
  Placement = pos=(4.158e-13,-136.97,87.59) rot=(0.57735,-0.57735,0.57735;2.0944rad)
  sketch-geometry (1):
    g0: Circle CenterX=4.16197 CenterY=-1.336e-13 CenterZ=0 NormalX=0 NormalY=0 NormalZ=1 AngleXU=0 Radius=1.60528
  constraints (2):
    c: Coincident(g0,g-3)
    c: Distance(g0,g-3) = 1
FEATURE [PartDesign::Pocket] Pocket006
  BaseFeature = -> Revolution
  Direction = (-7.3e-15,1,3.9e-15)
  Length = 5
  Length2 = 5
  Placement = pos=(0,-70.97,87.59) rot=(0.57735,-0.57735,0.57735;2.0944rad)
  Profile = -> Sketch021
  ReferenceAxis = -> Sketch021 [N_Axis]
  Refine = true
  Suppressed = false
  Type = 0
FEATURE [Sketcher::SketchObject] Sketch022
  ArcFitTolerance = 1e-06
  AttachmentSupport = -> [YZ_Plane]
  ExternalGeometry = -> [Pocket006]
  FullyConstrained = false
  MakeInternals = false
  MapMode = 5
  Placement = pos=(0,0,0) rot=(0.57735,0.57735,0.57735;2.0944rad)
  sketch-geometry (45):
    g0: LineSegment StartX=38.03 StartY=101.738 StartZ=0 EndX=40.6628 EndY=101.512 EndZ=0
    g1: LineSegment StartX=40.6628 StartY=101.512 StartZ=0 EndX=40.889 EndY=101.884 EndZ=0
    g2: LineSegment StartX=40.889 StartY=101.884 StartZ=0 EndX=44.4266 EndY=100.721 EndZ=0
    g3: LineSegment StartX=44.4266 StartY=100.721 StartZ=0 EndX=64.0492 EndY=98.7835 EndZ=0
    g4: LineSegment StartX=64.0492 StartY=98.7835 StartZ=0 EndX=73.8995 EndY=96.3029 EndZ=0
    g5: LineSegment StartX=73.8995 StartY=96.3029 StartZ=0 EndX=73.7557 EndY=95.0447 EndZ=0
    g6: LineSegment StartX=73.7557 StartY=95.0447 StartZ=0 EndX=93.2404 EndY=95.0447 EndZ=0
    g7: LineSegment StartX=93.2404 StartY=95.0447 StartZ=0 EndX=93.2785 EndY=95.9871 EndZ=0
    g8: LineSegment StartX=93.2785 StartY=95.9871 StartZ=0 EndX=97.11 EndY=96.71 EndZ=0
    g9: LineSegment StartX=38.03 StartY=79.7865 StartZ=0 EndX=67.2546 EndY=79.7865 EndZ=0
    g10: LineSegment StartX=67.2546 StartY=79.7865 StartZ=0 EndX=67.6295 EndY=80.4126 EndZ=0
    g11: LineSegment StartX=67.6295 StartY=80.4126 StartZ=0 EndX=74.6672 EndY=80.4126 EndZ=0
    g12-g16: GeomPoint [constr] x5 (B-spline internal-alignment scaffolding for g17; pole/knot coordinates omitted)
    g17: BSplineCurve PolesCount=7 KnotsCount=5 Degree=3 IsPeriodic=0
    g18-g24: Circle [constr] x7 (B-spline internal-alignment scaffolding for g17; pole/knot coordinates omitted)
    g25: LineSegment StartX=92.6209 StartY=59.8225 StartZ=0 EndX=92.4856 EndY=58.9585 EndZ=0
    g26: LineSegment StartX=92.4856 StartY=58.9585 StartZ=0 EndX=96.0588 EndY=58.4046 EndZ=0
    g27-g33: GeomPoint [constr] x7 (B-spline internal-alignment scaffolding for g34; pole/knot coordinates omitted)
    g34: BSplineCurve PolesCount=9 KnotsCount=7 Degree=3 IsPeriodic=0
    g35-g43: Circle [constr] x9 (B-spline internal-alignment scaffolding for g34; pole/knot coordinates omitted)
    g44: LineSegment StartX=38.03 StartY=101.738 StartZ=0 EndX=38.03 EndY=79.7865 EndZ=0
  constraints (56):
    c: PointOnObject(g0,g-6)
    c: Coincident(g0,g1)
    c: Coincident(g1,g2)
    c: Coincident(g2,g3)
    c: Coincident(g3,g4)
    c: Coincident(g4,g5)
    c: Coincident(g5,g6)
    c: Horizontal(g6)
    c: Coincident(g6,g7)
    c: Coincident(g7,g8)
    c: PointOnObject(g9,g-5)
    c: Horizontal(g9)
    c: Coincident(g9,g10)
    c: Coincident(g10,g11)
    c: Horizontal(g11)
    c: InternalAlignment(g12-g16 -> g17) x5
    c: InternalAlignment(g18,g17)
    c: Weight(g18) = 1
    c: InternalAlignment(g19,g17)
    c: Equal(g19,g18)
    c: InternalAlignment(g20,g17)
    c: Equal(g20,g18)
    c: InternalAlignment(g21,g17)
    c: Equal(g21,g18)
    c: InternalAlignment(g22,g17)
    c: Equal(g22,g18)
    c: InternalAlignment(g23,g17)
    c: Equal(g23,g18)
    c: InternalAlignment(g24,g17)
    c: Equal(g24,g18)
    c: Coincident(g12,g11)
    c: Coincident(g25,g17)
    c: Coincident(g25,g26)
    c: InternalAlignment(g27-g33 -> g34) x7
    c: InternalAlignment(g35,g34)
    c: Weight(g35) = 1
    c: InternalAlignment(g36,g34)
    c: Equal(g36,g35)
    c: InternalAlignment(g37,g34)
    c: Equal(g37,g35)
    c: InternalAlignment(g38,g34)
    c: Equal(g38,g35)
    c: InternalAlignment(g39,g34)
    c: Equal(g39,g35)
    c: InternalAlignment(g40,g34)
    c: Equal(g40,g35)
    c: InternalAlignment(g41,g34)
    c: Equal(g41,g35)
    c: InternalAlignment(g42,g34)
    c: Equal(g42,g35)
    c: InternalAlignment(g43,g34)
    c: Equal(g43,g35)
    c: Coincident(g27,g26)
    c: Coincident(g33,g8)
    c: Coincident(g0,g44)
    c: Coincident(g44,g9)
FEATURE [PartDesign::Pad] Pad015
  BaseFeature = -> Pocket006
  Direction = (1,0,0)
  Length = 7
  Length2 = 10
  Midplane = true
  Placement = pos=(0,-70.97,87.59) rot=(0.57735,-0.57735,0.57735;2.0944rad)
  Profile = -> Sketch022
  ReferenceAxis = -> Sketch022 [N_Axis]
  Refine = true
  Suppressed = false
  Type = 0
FEATURE [Sketcher::SketchObject] Sketch023
  ArcFitTolerance = 1e-06
  AttachmentSupport = -> [Pad015]
  ExternalGeometry = -> [Pad015]
  FullyConstrained = false
  MakeInternals = false
  MapMode = 5
  Placement = pos=(3.5,-70.97,87.59) rot=(0.707107,0,0.707107;3.14159rad)
  sketch-geometry (13):
    g0: LineSegment StartX=1.31628 StartY=-109 StartZ=0 EndX=1.31628 EndY=-143.012 EndZ=0
    g1: GeomPoint [constr] X=1.31628 Y=-143.012 Z=0
    g2: GeomPoint [constr] X=8.71823 Y=-144.91 Z=0
    g3: BSplineCurve PolesCount=4 KnotsCount=2 Degree=3 IsPeriodic=0
    g4-g7: Circle [constr] x4 (B-spline internal-alignment scaffolding for g3; pole/knot coordinates omitted)
    g8: LineSegment StartX=8.71823 StartY=-144.91 StartZ=0 EndX=7.4547 EndY=-164.21 EndZ=0
    g9: LineSegment StartX=7.4547 StartY=-164.21 StartZ=0 EndX=-27.7675 EndY=-163.591 EndZ=0
    g10: LineSegment StartX=-7.97553 StartY=-109 StartZ=0 EndX=1.31628 EndY=-109 EndZ=0
    g11: LineSegment StartX=-27.7675 StartY=-163.591 StartZ=0 EndX=-29.4271 EndY=-161.372 EndZ=0
    g12: LineSegment StartX=-29.4271 StartY=-161.372 StartZ=0 EndX=-7.97553 EndY=-109 EndZ=0
  constraints (21):
    c: PointOnObject(g0,g-3)
    c: Vertical(g0)
    c: InternalAlignment(g1,g3)
    c: InternalAlignment(g2,g3)
    c: InternalAlignment(g4,g3)
    c: Weight(g4) = 1
    c: InternalAlignment(g5,g3)
    c: Equal(g5,g4)
    c: InternalAlignment(g6,g3)
    c: Equal(g6,g4)
    c: InternalAlignment(g7,g3)
    c: Equal(g7,g4)
    c: Coincident(g1,g0)
    c: Coincident(g8,g3)
    c: Coincident(g8,g-5)
    c: Coincident(g8,g9)
    c: Coincident(g9,g-6)
    c: Coincident(g10,g0)
    c: Coincident(g9,g11)
    c: Coincident(g11,g12)
    c: Coincident(g12,g10)
FEATURE [PartDesign::Pocket] Pocket007
  BaseFeature = -> Pad015
  Direction = (-1,0,2e-16)
  Length = 1
  Length2 = 5
  Placement = pos=(0,-70.97,87.59) rot=(0.57735,-0.57735,0.57735;2.0944rad)
  Profile = -> Sketch023
  ReferenceAxis = -> Sketch023 [N_Axis]
  Refine = true
  Suppressed = false
  Type = 0
FEATURE [Sketcher::SketchObject] Sketch024
  ArcFitTolerance = 1e-06
  AttachmentSupport = -> [Pocket007]
  ExternalGeometry = -> [Pocket007]
  FullyConstrained = false
  MakeInternals = false
  MapMode = 5
  Placement = pos=(2.5,-70.97,87.59) rot=(0.707107,0,0.707107;3.14159rad)
  sketch-geometry (10):
    g0: LineSegment StartX=-7.17741 StartY=-138.599 StartZ=0 EndX=1.31628 EndY=-141.365 EndZ=0
    g1: LineSegment StartX=1.31628 StartY=-141.365 StartZ=0 EndX=1.31628 EndY=-143.012 EndZ=0
    g2: GeomPoint [constr] X=3.85199 Y=-144.045 Z=0
    g3: GeomPoint [constr] X=1.31628 Y=-143.012 Z=0
    g4: GeomPoint [constr] X=7.4547 Y=-144.734 Z=0
    g5: BSplineCurve PolesCount=4 KnotsCount=2 Degree=3 IsPeriodic=0
    g6-g9: Circle [constr] x4 (B-spline internal-alignment scaffolding for g5; pole/knot coordinates omitted)
  constraints (17):
    c: Coincident(g-5,g0)
    c: PointOnObject(g0,g-3)
    c: Coincident(g0,g1)
    c: Coincident(g1,g-4)
    c: PointOnObject(g2,g-4)
    c: InternalAlignment(g3,g5)
    c: InternalAlignment(g4,g5)
    c: InternalAlignment(g6,g5)
    c: Weight(g6) = 1
    c: InternalAlignment(g7,g5)
    c: Equal(g7,g6)
    c: InternalAlignment(g8,g5)
    c: Equal(g8,g6)
    c: InternalAlignment(g9,g5)
    c: Equal(g9,g6)
    c: Coincident(g3,g1)
    c: Coincident(g4,g-4)
FEATURE [PartDesign::Mirrored] Mirrored003
  BaseFeature = -> Pocket007
  MirrorPlane = -> YZ_Plane
  Originals = -> [Pocket007]
  Placement = pos=(0,-70.97,87.59) rot=(0.57735,-0.57735,0.57735;2.0944rad)
  Refine = true
  Suppressed = false
  TransformMode = 0
FEATURE [Sketcher::SketchObject] Sketch025
  ArcFitTolerance = 1e-06
  AttachmentSupport = -> [Mirrored003]
  FullyConstrained = false
  MakeInternals = false
  MapMode = 5
  Placement = pos=(4.62,-70.97,87.59) rot=(0.707107,0,0.707107;3.14159rad)
  sketch-geometry (4):
    g0: LineSegment StartX=1.53958 StartY=-0.597724 StartZ=0 EndX=1.53958 EndY=-25.0856 EndZ=0
    g1: LineSegment StartX=1.53958 StartY=-25.0856 StartZ=0 EndX=6.68924 EndY=-25.0856 EndZ=0
    g2: LineSegment StartX=6.68924 StartY=-25.0856 StartZ=0 EndX=6.68924 EndY=-0.597724 EndZ=0
    g3: LineSegment StartX=6.68924 StartY=-0.597724 StartZ=0 EndX=1.53958 EndY=-0.597724 EndZ=0
  constraints (8):
    c: Coincident(g0,g1)
    c: Coincident(g1,g2)
    c: Coincident(g2,g3)
    c: Coincident(g3,g0)
    c: Vertical(g0)
    c: Vertical(g2)
    c: Horizontal(g1)
    c: Horizontal(g3)
FEATURE [PartDesign::Pad] Pad016
  BaseFeature = -> Mirrored003
  Direction = (1,6e-15,8e-15)
  Length = 2
  Length2 = 10
  Placement = pos=(0,-70.97,87.59) rot=(0.57735,-0.57735,0.57735;2.0944rad)
  Profile = -> Sketch025
  ReferenceAxis = -> Sketch025 [N_Axis]
  Refine = true
  Suppressed = false
  Type = 0
FEATURE [Sketcher::SketchObject] Sketch026
  ArcFitTolerance = 1e-06
  AttachmentSupport = -> [Pad016]
  FullyConstrained = true
  MakeInternals = false
  MapMode = 5
  Placement = pos=(-3.5e-15,-70.3723,87.59) rot=(0.57735,-0.57735,0.57735;2.0944rad)
FEATURE [PartDesign::Chamfer] Chamfer
  Angle = 30
  Base = -> Pad016 [Edge522,Edge526]
  BaseFeature = -> Pad016
  ChamferType = 2
  FlipDirection = false
  Placement = pos=(0,-70.97,87.59) rot=(0.57735,-0.57735,0.57735;2.0944rad)
  Refine = true
  Size = 0.5
  Size2 = 1
  SupportTransform = false
  Suppressed = false
  UseAllEdges = false
FEATURE [Sketcher::SketchObject] Sketch027
  ArcFitTolerance = 1e-06
  AttachmentSupport = -> [Chamfer]
  ExternalGeometry = -> [Chamfer]
  FullyConstrained = false
  MakeInternals = false
  MapMode = 5
  Placement = pos=(-5.34e-14,-70.97,94.2792) rot=(0,0,1;3.14159rad)
  sketch-geometry (8):
    g0: LineSegment StartX=-7.80098 StartY=-1.59772 StartZ=0 EndX=-7.80098 EndY=-2.59772 EndZ=0
    g1: LineSegment StartX=-7.80098 StartY=-2.59772 StartZ=0 EndX=-5.17243 EndY=-2.59772 EndZ=0
    g2: LineSegment StartX=-5.17243 StartY=-2.59772 StartZ=0 EndX=-5.17243 EndY=-1.59772 EndZ=0
    g3: LineSegment StartX=-5.17243 StartY=-1.59772 StartZ=0 EndX=-7.80098 EndY=-1.59772 EndZ=0
    g4: LineSegment StartX=7.80098 StartY=-1.59772 StartZ=0 EndX=7.80098 EndY=-2.59772 EndZ=0
    g5: LineSegment StartX=7.80098 StartY=-2.59772 StartZ=0 EndX=5.17243 EndY=-2.59772 EndZ=0
    g6: LineSegment StartX=5.17243 StartY=-2.59772 StartZ=0 EndX=5.17243 EndY=-1.59772 EndZ=0
    g7: LineSegment StartX=5.17243 StartY=-1.59772 StartZ=0 EndX=7.80098 EndY=-1.59772 EndZ=0
  constraints (18):
    c: Coincident(g0,g1)
    c: Coincident(g1,g2)
    c: Coincident(g2,g3)
    c: Coincident(g3,g0)
    c: Vertical(g0)
    c: Vertical(g2)
    c: Horizontal(g1)
    c: Horizontal(g3)
    c: Distance(g3,g-3) = 1
    c: DistanceY(g0,g0) = 1
    c: Coincident(g4,g5)
    c: Coincident(g5,g6)
    c: Coincident(g6,g7)
    c: Coincident(g7,g4)
    c: Vertical(g4)
    c: Vertical(g6)
    c: Horizontal(g5)
    c: Horizontal(g7)
FEATURE [PartDesign::Mirrored] Mirrored004
  BaseFeature = -> Chamfer
  MirrorPlane = -> YZ_Plane
  Originals = -> [Pad016,Chamfer]
  Placement = pos=(0,-70.97,87.59) rot=(0.57735,-0.57735,0.57735;2.0944rad)
  Refine = true
  Suppressed = false
  TransformMode = 0
FEATURE [PartDesign::Pocket] Pocket008
  BaseFeature = -> Mirrored004
  Direction = (8.4e-15,0,-1)
  Length = 5
  Length2 = 5
  Placement = pos=(0,-70.97,87.59) rot=(0.57735,-0.57735,0.57735;2.0944rad)
  Profile = -> Sketch027
  ReferenceAxis = -> Sketch027 [N_Axis]
  Refine = true
  Suppressed = false
  Type = 1
FEATURE [PartDesign::LinearPattern] LinearPattern001
  BaseFeature = -> Pocket008
  Direction = -> Pocket008 [Edge38]
  Length = 22
  Mode = 1
  Occurrences = 12
  Offset = 2
  Originals = -> [Pocket008]
  Placement = pos=(0,-70.97,87.59) rot=(0.57735,-0.57735,0.57735;2.0944rad)
  Refine = true
  Reversed = true
  Suppressed = false
  TransformMode = 0
FEATURE [Sketcher::SketchObject] Sketch028
  ArcFitTolerance = 1e-06
  AttachmentSupport = -> [LinearPattern001]
  ExternalGeometry = -> [LinearPattern001]
  FullyConstrained = true
  MakeInternals = false
  MapMode = 5
  Placement = pos=(0,-70.97,88.77) rot=(1,0,0;3.14159rad)
  sketch-geometry (4):
    g0: LineSegment StartX=2.51 StartY=0 StartZ=0 EndX=-2.51 EndY=0 EndZ=0
    g1: LineSegment StartX=-2.51 StartY=0 StartZ=0 EndX=-2.51 EndY=-44.295 EndZ=0
    g2: LineSegment StartX=-2.51 StartY=-44.295 StartZ=0 EndX=2.51 EndY=-44.295 EndZ=0
    g3: LineSegment StartX=2.51 StartY=-44.295 StartZ=0 EndX=2.51 EndY=0 EndZ=0
  constraints (10):
    c: Coincident(g0,g1)
    c: Coincident(g1,g2)
    c: Coincident(g2,g3)
    c: Coincident(g3,g0)
    c: Horizontal(g0)
    c: Vertical(g1)
    c: Vertical(g3)
    c: Coincident(g0,g-4)
    c: PointOnObject(g1,g-3)
    c: Tangent(g2,g-5)
FEATURE [PartDesign::Pad] Pad017
  BaseFeature = -> LinearPattern001
  Direction = (6.7e-15,4.4e-15,-1)
  Length = 3
  Length2 = 10
  Placement = pos=(0,-70.97,87.59) rot=(0.57735,-0.57735,0.57735;2.0944rad)
  Profile = -> Sketch028
  ReferenceAxis = -> Sketch028 [N_Axis]
  Refine = true
  Suppressed = false
  Type = 0
FEATURE [Sketcher::SketchObject] Sketch029
  ArcFitTolerance = 1e-06
  AttachmentSupport = -> [Pad017]
  ExternalGeometry = -> [Pad017]
  FullyConstrained = false
  MakeInternals = false
  MapMode = 5
  Placement = pos=(0,-70.97,87.59) rot=(0.57735,-0.57735,0.57735;2.0944rad)
  sketch-geometry (8):
    g0: LineSegment StartX=-0.932178 StartY=2.51 StartZ=0 EndX=-1.82 EndY=1.70514 EndZ=0
    g1: LineSegment StartX=-1.82 StartY=1.70514 StartZ=0 EndX=-2.71408 EndY=2.44095 EndZ=0
    g2: LineSegment StartX=-2.71408 StartY=2.44095 StartZ=0 EndX=-1.64139 EndY=3.20335 EndZ=0
    g3: LineSegment StartX=-1.64139 StartY=3.20335 StartZ=0 EndX=-0.932178 EndY=2.51 EndZ=0
    g4: LineSegment StartX=-0.932178 StartY=-2.51 StartZ=0 EndX=-1.82 EndY=-1.70514 EndZ=0
    g5: LineSegment StartX=-1.82 StartY=-1.70514 StartZ=0 EndX=-2.71408 EndY=-2.44095 EndZ=0
    g6: LineSegment StartX=-2.71408 StartY=-2.44095 StartZ=0 EndX=-1.64139 EndY=-3.20335 EndZ=0
    g7: LineSegment StartX=-1.64139 StartY=-3.20335 StartZ=0 EndX=-0.932178 EndY=-2.51 EndZ=0
  constraints (10):
    c: PointOnObject(g0,g-3)
    c: PointOnObject(g0,g-5)
    c: Coincident(g0,g1)
    c: Coincident(g1,g2)
    c: Coincident(g2,g3)
    c: Coincident(g3,g0)
    c: Coincident(g4,g5)
    c: Coincident(g5,g6)
    c: Coincident(g6,g7)
    c: Coincident(g7,g4)
FEATURE [PartDesign::Pocket] Pocket009
  BaseFeature = -> Pad017
  Direction = (-6.3e-15,1,9.7e-15)
  Length = 0
  Length2 = 5
  Placement = pos=(0,-70.97,87.59) rot=(0.57735,-0.57735,0.57735;2.0944rad)
  Profile = -> Sketch029
  ReferenceAxis = -> Sketch029 [N_Axis]
  Refine = true
  Suppressed = false
  Type = 3
  UpToFace = -> Pad017 [Face121]
FEATURE [Sketcher::SketchObject] Sketch030
  ArcFitTolerance = 1e-06
  AttachmentSupport = -> [Pocket009]
  ExternalGeometry = -> [Pocket009]
  FullyConstrained = true
  MakeInternals = false
  MapMode = 5
  Placement = pos=(-2.51,-70.97,87.59) rot=(0.707107,0,-0.707107;3.14159rad)
  sketch-geometry (4):
    g0: LineSegment StartX=1.82 StartY=-1 StartZ=0 EndX=0.82 EndY=-1 EndZ=0
    g1: LineSegment StartX=0.82 StartY=-1 StartZ=0 EndX=0.82 EndY=-2 EndZ=0
    g2: LineSegment StartX=0.82 StartY=-2 StartZ=0 EndX=1.82 EndY=-2 EndZ=0
    g3: LineSegment StartX=1.82 StartY=-2 StartZ=0 EndX=1.82 EndY=-1 EndZ=0
  constraints (12):
    c: Coincident(g0,g1)
    c: Coincident(g1,g2)
    c: Coincident(g2,g3)
    c: Coincident(g3,g0)
    c: Horizontal(g0)
    c: Horizontal(g2)
    c: Vertical(g1)
    c: Vertical(g3)
    c: PointOnObject(g0,g-3)
    c: Distance(g-3,g0) = 1
    c: DistanceX(g2,g2) = 1
    c: DistanceY(g3,g3) = 1
FEATURE [PartDesign::Pocket] Pocket010
  BaseFeature = -> Pocket009
  Direction = (1,0,7.4e-15)
  Length = 5
  Length2 = 5
  Placement = pos=(0,-70.97,87.59) rot=(0.57735,-0.57735,0.57735;2.0944rad)
  Profile = -> Sketch030
  ReferenceAxis = -> Sketch030 [N_Axis]
  Refine = true
  Suppressed = false
  Type = 1
FEATURE [PartDesign::LinearPattern] LinearPattern002
  BaseFeature = -> Pocket010
  Direction = -> Y_Axis
  Length = 40
  Mode = 1
  Occurrences = 21
  Offset = 2
  Originals = -> [Pocket010]
  Placement = pos=(0,-70.97,87.59) rot=(0.57735,-0.57735,0.57735;2.0944rad)
  Refine = true
  Suppressed = false
  TransformMode = 0
FEATURE [Sketcher::SketchObject] Sketch031
  ArcFitTolerance = 1e-06
  AttachmentSupport = -> [XZ_Plane]
  ExternalGeometry = -> [LinearPattern002]
  FullyConstrained = false
  MakeInternals = false
  MapMode = 5
  Placement = pos=(0,0,0) rot=(1,0,0;1.5708rad)
  sketch-geometry (21):
    g0: LineSegment [constr] StartX=3.62 StartY=80 StartZ=0 EndX=73.3006 EndY=80 EndZ=0
    g1: LineSegment StartX=3.62 StartY=80 StartZ=0 EndX=3.62 EndY=82 EndZ=0
    g2: LineSegment StartX=3.62 StartY=82 StartZ=0 EndX=11.62 EndY=82 EndZ=0
    g3: LineSegment StartX=11.62 StartY=82 StartZ=0 EndX=11.62 EndY=89 EndZ=0
    g4: LineSegment StartX=11.62 StartY=89 StartZ=0 EndX=23.73 EndY=89 EndZ=0
    g5: LineSegment StartX=23.73 StartY=89 StartZ=0 EndX=23.73 EndY=87 EndZ=0
    g6: LineSegment StartX=23.73 StartY=87 StartZ=0 EndX=32.73 EndY=87 EndZ=0
    g7: LineSegment StartX=32.73 StartY=87 StartZ=0 EndX=32.73 EndY=80 EndZ=0
    g8: LineSegment StartX=32.73 StartY=80 StartZ=0 EndX=3.62 EndY=80 EndZ=0
    g9: LineSegment [constr] StartX=-3.62 StartY=80 StartZ=0 EndX=-73.3006 EndY=80 EndZ=0
    g10: LineSegment StartX=-3.62 StartY=80 StartZ=0 EndX=-3.62 EndY=82 EndZ=0
    g11: LineSegment StartX=-3.62 StartY=82 StartZ=0 EndX=-11.62 EndY=82 EndZ=0
    g12: LineSegment StartX=-11.62 StartY=82 StartZ=0 EndX=-11.62 EndY=89 EndZ=0
    g13: LineSegment StartX=-11.62 StartY=89 StartZ=0 EndX=-23.73 EndY=89 EndZ=0
    g14: LineSegment StartX=-23.73 StartY=80 StartZ=0 EndX=-3.62 EndY=80 EndZ=0
    g15: LineSegment StartX=-23.73 StartY=89 StartZ=0 EndX=-23.73 EndY=95.6254 EndZ=0
    g16: LineSegment StartX=-27.0044 StartY=98.8998 StartZ=0 EndX=-28.73 EndY=98.8998 EndZ=0
    g17: LineSegment StartX=-28.73 StartY=98.8998 StartZ=0 EndX=-28.73 EndY=80 EndZ=0
    g18: LineSegment StartX=-28.73 StartY=80 StartZ=0 EndX=-23.73 EndY=80 EndZ=0
    g19: ArcOfCircle CenterX=-27.0044 CenterY=95.6254 CenterZ=0 NormalX=0 NormalY=0 NormalZ=1 AngleXU=0 Radius=3.27437 StartAngle=1e-16 EndAngle=1.5708
    g20: GeomPoint [constr] X=-23.73 Y=98.8998 Z=0
  constraints (55):
    c: PointOnObject(g0,g-3)
    c: Horizontal(g0)
    c: Distance(g-1,g0) = 80
    c: Coincident(g0,g1)
    c: PointOnObject(g1,g-3)
    c: Coincident(g1,g2)
    c: Horizontal(g2)
    c: Coincident(g2,g3)
    c: Vertical(g3)
    c: Coincident(g3,g4)
    c: Horizontal(g4)
    c: Coincident(g4,g5)
    c: Vertical(g5)
    c: Coincident(g5,g6)
    c: Horizontal(g6)
    c: Coincident(g6,g7)
    c: PointOnObject(g7,g0)
    c: Coincident(g8,g7)
    c: Coincident(g8,g0)
    c: Distance(g2,g0) = 2
    c: DistanceY(g3,g3) = 7
    c: Distance(g4,g-2) = 23.73
    c: Distance(g6,g6) = 9
    c: Vertical(g7)
    c: DistanceY(g7,g7) = 7
    c: DistanceX(g2,g2) = 8
    c: Horizontal(g9)
    c: Coincident(g9,g10)
    c: Coincident(g10,g11)
    c: Horizontal(g11)
    c: Coincident(g11,g12)
    c: Vertical(g12)
    c: Coincident(g12,g13)
    c: Horizontal(g13)
    c: PointOnObject(g14,g9)
    c: Coincident(g14,g9)
    c: Distance(g11,g9) = 2
    c: Distance(g-1,g9) = 80
    c: Tangent(g10,g-4)
    c: DistanceY(g12,g12) = 7
    c: DistanceX(g11,g11) = 8
    c: DistanceX(g13,g-1) = 23.73
    c: Coincident(g13,g15)
    c: Vertical(g15)
    c: Horizontal(g16)
    c: Coincident(g16,g17)
    c: PointOnObject(g17,g9)
    c: Vertical(g17)
    c: Coincident(g17,g18)
    c: Coincident(g18,g14)
    c: Distance(g16,g-2) = 28.73
    c: PointOnObject(g20,g15)
    c: PointOnObject(g20,g16)
    c: Tangent(g15,g19) = -1.5708
    c: Tangent(g16,g19) = -1.5708
FEATURE [PartDesign::Revolution] Revolution001
  Angle = 360
  Angle2 = 60
  Axis = (69.6806,0,0)
  Base = (3.62,1.78e-14,80)
  BaseFeature = -> LinearPattern002
  Placement = pos=(0,-70.97,87.59) rot=(0.57735,-0.57735,0.57735;2.0944rad)
  Profile = -> Sketch031
  ReferenceAxis = -> Sketch031 [Axis]
  Refine = true
  Suppressed = false
  Type = 0
FEATURE [PartDesign::Plane] DatumPlane001
  AttachmentOffset = pos=(0,0,77) rot=(0,0,1;0rad)
  AttachmentSupport = -> [XY_Plane]
  Length = 97.5309
  MapMode = 5
  Placement = pos=(0,0,77) rot=(0,0,1;0rad)
  ResizeMode = 0
  Width = 260.825
FEATURE [Sketcher::SketchObject] Sketch032
  ArcFitTolerance = 1e-06
  AttachmentSupport = -> [DatumPlane001]
  ExternalGeometry = -> [Revolution001]
  FullyConstrained = false
  MakeInternals = false
  MapMode = 5
  Placement = pos=(0,0,77) rot=(0,0,1;0rad)
  sketch-geometry (5):
    g0: LineSegment StartX=0 StartY=-68 StartZ=0 EndX=-16.73 EndY=-68 EndZ=0
    g1: LineSegment StartX=-16.73 StartY=-68 StartZ=0 EndX=-23.73 EndY=-51 EndZ=0
    g2: LineSegment [constr] StartX=-23.73 StartY=-9 StartZ=0 EndX=-23.73 EndY=-164.884 EndZ=0
    g3: LineSegment StartX=-23.73 StartY=-51 StartZ=0 EndX=0 EndY=-51 EndZ=0
    g4: LineSegment StartX=0 StartY=-51 StartZ=0 EndX=0 EndY=-68 EndZ=0
  constraints (14):
    c: PointOnObject(g0,g-2)
    c: Horizontal(g0)
    c: Coincident(g0,g1)
    c: Coincident(g2,g-6)
    c: Vertical(g2)
    c: PointOnObject(g1,g2)
    c: Distance(g-1,g0) = 68
    c: Distance(g0,g2) = 7
    c: Coincident(g1,g3)
    c: PointOnObject(g3,g-2)
    c: Horizontal(g3)
    c: Coincident(g3,g4)
    c: Coincident(g4,g0)
    c: DistanceY(g4,g4) = 17
FEATURE [Sketcher::SketchObject] Sketch033
  ArcFitTolerance = 1e-06
  AttachmentSupport = -> [DatumPlane001]
  FullyConstrained = false
  MakeInternals = false
  MapMode = 5
  Placement = pos=(0,0,77) rot=(0,0,1;0rad)
  sketch-geometry (4):
    g0: LineSegment StartX=0 StartY=-56.8416 StartZ=0 EndX=-3.84249 EndY=-56.8416 EndZ=0
    g1: LineSegment StartX=-3.84249 StartY=-56.8416 StartZ=0 EndX=-3.84249 EndY=-64.3954 EndZ=0
    g2: LineSegment StartX=-3.84249 StartY=-64.3954 StartZ=0 EndX=0 EndY=-64.3954 EndZ=0
    g3: LineSegment StartX=0 StartY=-64.3954 StartZ=0 EndX=0 EndY=-56.8416 EndZ=0
  constraints (8):
    c: Coincident(g0,g1)
    c: Coincident(g1,g2)
    c: Coincident(g2,g3)
    c: Coincident(g3,g0)
    c: Horizontal(g0)
    c: Horizontal(g2)
    c: Vertical(g1)
    c: Tangent(g3,g-2)
FEATURE [PartDesign::Pad] Pad018
  BaseFeature = -> Revolution001
  Direction = (0,0,1)
  Length = 14
  Length2 = 10
  Placement = pos=(0,-70.97,87.59) rot=(0.57735,-0.57735,0.57735;2.0944rad)
  Profile = -> Sketch033
  ReferenceAxis = -> Sketch033 [N_Axis]
  Refine = true
  Suppressed = false
  Type = 0
FEATURE [PartDesign::Pad] Pad019
  BaseFeature = -> Pad018
  Direction = (0,0,1)
  Length = 5
  Length2 = 10
  Placement = pos=(0,-70.97,87.59) rot=(0.57735,-0.57735,0.57735;2.0944rad)
  Profile = -> Sketch032
  ReferenceAxis = -> Sketch032 [N_Axis]
  Refine = true
  Reversed = true
  Suppressed = false
  Type = 0
FEATURE [PartDesign::Plane] DatumPlane002
  AttachmentOffset = pos=(0,0,8) rot=(0,0,1;0rad)
  AttachmentSupport = -> [XZ_Plane]
  Length = 92.8021
  MapMode = 5
  Placement = pos=(0,-8,1.8e-15) rot=(1,0,0;1.5708rad)
  ResizeMode = 0
  Width = 178.251
FEATURE [Sketcher::SketchObject] Sketch034
  ArcFitTolerance = 1e-06
  AttachmentSupport = -> [DatumPlane002]
  ExternalGeometry = -> [Pad019]
  FullyConstrained = false
  MakeInternals = false
  MapMode = 5
  Placement = pos=(0,-8,1.8e-15) rot=(1,0,0;1.5708rad)
  sketch-geometry (4):
    g0: LineSegment StartX=-23.73 StartY=77.1247 StartZ=0 EndX=-12.62 EndY=77.1247 EndZ=0
    g1: LineSegment StartX=-12.62 StartY=77.1247 StartZ=0 EndX=-12.62 EndY=101.546 EndZ=0
    g2: LineSegment StartX=-12.62 StartY=101.546 StartZ=0 EndX=-23.73 EndY=101.546 EndZ=0
    g3: LineSegment StartX=-23.73 StartY=101.546 StartZ=0 EndX=-23.73 EndY=77.1247 EndZ=0
  constraints (10):
    c: Coincident(g0,g1)
    c: Coincident(g1,g2)
    c: Coincident(g2,g3)
    c: Coincident(g3,g0)
    c: Horizontal(g0)
    c: Horizontal(g2)
    c: Vertical(g1)
    c: Vertical(g3)
    c: PointOnObject(g0,g-3)
    c: Distance(g-4,g1) = 1
FEATURE [PartDesign::Pad] Pad020
  BaseFeature = -> Pad019
  Direction = (0,-1,2e-16)
  Length = 3
  Length2 = 10
  Placement = pos=(0,-70.97,87.59) rot=(0.57735,-0.57735,0.57735;2.0944rad)
  Profile = -> Sketch034
  ReferenceAxis = -> Sketch034 [N_Axis]
  Refine = true
  Suppressed = false
  Type = 0
FEATURE [Sketcher::SketchObject] Sketch035
  ArcFitTolerance = 1e-06
  AttachmentSupport = -> [Pad020]
  ExternalGeometry = -> [Pad020]
  FullyConstrained = true
  MakeInternals = false
  MapMode = 5
  Placement = pos=(2.2e-15,-51,87.59) rot=(0.57735,0.57735,0.57735;4.18879rad)
  sketch-geometry (4):
    g0: LineSegment StartX=-10.59 StartY=-23.73 StartZ=0 EndX=-10.59 EndY=-16.73 EndZ=0
    g1: LineSegment StartX=-10.59 StartY=-16.73 StartZ=0 EndX=-15.59 EndY=-16.73 EndZ=0
    g2: LineSegment StartX=-15.59 StartY=-16.73 StartZ=0 EndX=-15.59 EndY=-23.73 EndZ=0
    g3: LineSegment StartX=-15.59 StartY=-23.73 StartZ=0 EndX=-10.59 EndY=-23.73 EndZ=0
  constraints (11):
    c: Coincident(g0,g1)
    c: Coincident(g1,g2)
    c: Coincident(g2,g3)
    c: Coincident(g3,g0)
    c: Vertical(g0)
    c: Vertical(g2)
    c: Horizontal(g1)
    c: Horizontal(g3)
    c: Coincident(g0,g-4)
    c: PointOnObject(g1,g-5)
    c: DistanceY(g2,g2) = 7
FEATURE [Sketcher::SketchObject] Sketch036
  ArcFitTolerance = 1e-06
  AttachmentSupport = -> [Pad020]
  ExternalGeometry = -> [Pad020]
  FullyConstrained = false
  MakeInternals = false
  MapMode = 5
  Placement = pos=(0,-11,87.59) rot=(0.57735,-0.57735,0.57735;2.0944rad)
  sketch-geometry (4):
    g0: LineSegment StartX=13.9562 StartY=23.73 StartZ=0 EndX=-0.472301 EndY=23.73 EndZ=0
    g1: LineSegment StartX=-0.472301 StartY=23.73 StartZ=0 EndX=-0.472301 EndY=12.62 EndZ=0
    g2: LineSegment StartX=-0.472301 StartY=12.62 StartZ=0 EndX=13.9562 EndY=12.62 EndZ=0
    g3: LineSegment StartX=13.9562 StartY=12.62 StartZ=0 EndX=13.9562 EndY=23.73 EndZ=0
  constraints (10):
    c: Coincident(g0,g1)
    c: Coincident(g1,g2)
    c: Coincident(g2,g3)
    c: Coincident(g3,g0)
    c: Horizontal(g0)
    c: Horizontal(g2)
    c: Vertical(g1)
    c: Vertical(g3)
    c: Coincident(g0,g-3)
    c: PointOnObject(g1,g-4)
FEATURE [PartDesign::AdditiveLoft] AdditiveLoft
  BaseFeature = -> Pad020
  Closed = false
  Placement = pos=(0,-70.97,87.59) rot=(0.57735,-0.57735,0.57735;2.0944rad)
  Profile = -> Sketch036
  Refine = true
  Ruled = false
  Sections = -> [Sketch035]
  Suppressed = false
FEATURE [Sketcher::SketchObject] Sketch037
  ArcFitTolerance = 1e-06
  AttachmentSupport = -> [AdditiveLoft]
  ExternalGeometry = -> [AdditiveLoft]
  FullyConstrained = true
  MakeInternals = false
  MapMode = 5
  Placement = pos=(0,-70.97,72) rot=(1,0,0;3.14159rad)
  sketch-geometry (1):
    g0: Circle CenterX=-16.73 CenterY=-2.97 CenterZ=0 NormalX=0 NormalY=0 NormalZ=1 AngleXU=0 Radius=2
  constraints (2):
    c: Coincident(g0,g-3)
    c: Diameter(g0) = 4
FEATURE [PartDesign::Pad] Pad021
  BaseFeature = -> AdditiveLoft
  Direction = (0,0,-1)
  Length = 10
  Length2 = 10
  Placement = pos=(0,-70.97,87.59) rot=(0.57735,-0.57735,0.57735;2.0944rad)
  Profile = -> Sketch037
  ReferenceAxis = -> Sketch037 [N_Axis]
  Refine = true
  Reversed = true
  Suppressed = false
  Type = 3
  UpToFace = -> AdditiveLoft [Face66]
FEATURE [Sketcher::SketchObject] Sketch038
  ArcFitTolerance = 1e-06
  AttachmentSupport = -> [Pad021]
  ExternalGeometry = -> [Pad021]
  FullyConstrained = true
  MakeInternals = false
  MapMode = 5
  Placement = pos=(-9.4e-15,-70.97,101.546) rot=(0,0,1;3.14159rad)
  sketch-geometry (4):
    g0: ArcOfCircle CenterX=16.73 CenterY=-2.97 CenterZ=0 NormalX=0 NormalY=0 NormalZ=1 AngleXU=0 Radius=3 StartAngle=1e-16 EndAngle=3.14159
    g1: ArcOfCircle CenterX=16.73 CenterY=-59.97 CenterZ=0 NormalX=0 NormalY=0 NormalZ=1 AngleXU=0 Radius=3 StartAngle=3.14159 EndAngle=6.28319
    g2: LineSegment StartX=19.73 StartY=-2.97 StartZ=0 EndX=19.73 EndY=-59.97 EndZ=0
    g3: LineSegment StartX=13.73 StartY=-2.97 StartZ=0 EndX=13.73 EndY=-59.97 EndZ=0
  constraints (9):
    c: Tangent(g0,g2) = 1.5708
    c: Tangent(g0,g3) = -1.5708
    c: Tangent(g1,g2) = 1.5708
    c: Tangent(g1,g3) = -1.5708
    c: Equal(g0,g1)
    c: Coincident(g0,g-3)
    c: Vertical(g2)
    c: Tangent(g1,g-4)
    c: Distance(g0,g-3) = 1
FEATURE [PartDesign::Pad] Pad022
  BaseFeature = -> Pad021
  Direction = (-1.1e-15,0,1)
  Length = 3
  Length2 = 10
  Placement = pos=(0,-70.97,87.59) rot=(0.57735,-0.57735,0.57735;2.0944rad)
  Profile = -> Sketch038
  ReferenceAxis = -> Sketch038 [N_Axis]
  Refine = true
  Reversed = true
  Suppressed = false
  Type = 0
FEATURE [PartDesign::Mirrored] Mirrored005
  BaseFeature = -> Pad022
  MirrorPlane = -> Sketch038 [V_Axis]
  Originals = -> [Pad022,Pad021,AdditiveLoft,Pad020,Pad019,Pad018]
  Placement = pos=(0,-70.97,87.59) rot=(0.57735,-0.57735,0.57735;2.0944rad)
  Refine = true
  Suppressed = false
  TransformMode = 0
FEATURE [PartDesign::Plane] DatumPlane003
  AttachmentOffset = pos=(0,0,-27) rot=(0,0,1;0rad)
  AttachmentSupport = -> [YZ_Plane]
  Length = 273.301
  MapMode = 5
  Placement = pos=(-27,0,0) rot=(0.57735,0.57735,0.57735;2.0944rad)
  ResizeMode = 0
  Width = 195.457
FEATURE [Sketcher::SketchObject] Sketch039
  ArcFitTolerance = 1e-06
  AttachmentSupport = -> [DatumPlane003]
  FullyConstrained = false
  MakeInternals = false
  MapMode = 5
  Placement = pos=(-27,0,0) rot=(0.57735,0.57735,0.57735;2.0944rad)
  sketch-geometry (4):
    g0: LineSegment StartX=-7.55309 StartY=68.9554 StartZ=0 EndX=-7.55309 EndY=64.2268 EndZ=0
    g1: LineSegment StartX=-7.55309 StartY=64.2268 StartZ=0 EndX=7.3541 EndY=64.2268 EndZ=0
    g2: LineSegment StartX=7.3541 StartY=64.2268 StartZ=0 EndX=7.3541 EndY=68.9554 EndZ=0
    g3: LineSegment StartX=7.3541 StartY=68.9554 StartZ=0 EndX=-7.55309 EndY=68.9554 EndZ=0
  constraints (8):
    c: Coincident(g0,g1)
    c: Coincident(g1,g2)
    c: Coincident(g2,g3)
    c: Coincident(g3,g0)
    c: Vertical(g0)
    c: Vertical(g2)
    c: Horizontal(g1)
    c: Horizontal(g3)
FEATURE [Sketcher::SketchObject] Sketch040
  ArcFitTolerance = 1e-06
  AttachmentSupport = -> [XZ_Plane]
  ExternalGeometry = -> [Mirrored005]
  FullyConstrained = false
  MakeInternals = false
  MapMode = 5
  Placement = pos=(0,0,0) rot=(1,0,0;1.5708rad)
  sketch-geometry (21):
    g0: LineSegment StartX=-23.73 StartY=95.6254 StartZ=0 EndX=-20.6948 EndY=95.6254 EndZ=0
    g1: LineSegment StartX=-20.6948 StartY=95.6254 StartZ=0 EndX=-20.6948 EndY=119.552 EndZ=0
    g2: LineSegment StartX=-21.3049 StartY=120.162 StartZ=0 EndX=-25.0086 EndY=120.162 EndZ=0
    g3: LineSegment StartX=-25.0086 StartY=120.162 StartZ=0 EndX=-25.0086 EndY=126.997 EndZ=0
    g4: LineSegment StartX=-26.1344 StartY=128.123 StartZ=0 EndX=-33.4215 EndY=128.123 EndZ=0
    g5: LineSegment StartX=-33.9761 StartY=128.677 StartZ=0 EndX=-33.9761 EndY=132.044 EndZ=0
    g6: LineSegment StartX=-33.9761 StartY=132.044 StartZ=0 EndX=-38.8649 EndY=132.044 EndZ=0
    g7: LineSegment StartX=-38.8649 StartY=132.044 StartZ=0 EndX=-38.8649 EndY=126.509 EndZ=0
    g8: LineSegment StartX=-37.9532 StartY=125.598 StartZ=0 EndX=-29.8242 EndY=125.598 EndZ=0
    g9: LineSegment StartX=-28.3351 StartY=124.108 StartZ=0 EndX=-28.3351 EndY=95.6254 EndZ=0
    g10: LineSegment StartX=-28.3351 StartY=95.6254 StartZ=0 EndX=-23.73 EndY=95.6254 EndZ=0
    g11: ArcOfCircle CenterX=-26.1344 CenterY=126.997 CenterZ=0 NormalX=0 NormalY=0 NormalZ=1 AngleXU=0 Radius=1.12578 StartAngle=0 EndAngle=1.5708
    g12: GeomPoint [constr] X=-25.0086 Y=128.123 Z=0
    g13: ArcOfCircle CenterX=-21.3049 CenterY=119.552 CenterZ=0 NormalX=0 NormalY=0 NormalZ=1 AngleXU=0 Radius=0.610057 StartAngle=0 EndAngle=1.5708
    g14: GeomPoint [constr] X=-20.6948 Y=120.162 Z=0
    g15: ArcOfCircle CenterX=-29.8242 CenterY=124.108 CenterZ=0 NormalX=0 NormalY=0 NormalZ=1 AngleXU=0 Radius=1.48914 StartAngle=0 EndAngle=1.5708
    g16: GeomPoint [constr] X=-28.3351 Y=125.598 Z=0
    g17: ArcOfCircle CenterX=-37.9532 CenterY=126.509 CenterZ=0 NormalX=0 NormalY=0 NormalZ=1 AngleXU=0 Radius=0.911718 StartAngle=3.14159 EndAngle=4.71239
    g18: GeomPoint [constr] X=-38.8649 Y=125.598 Z=0
    g19: ArcOfCircle CenterX=-33.4215 CenterY=128.677 CenterZ=0 NormalX=0 NormalY=0 NormalZ=1 AngleXU=0 Radius=0.554628 StartAngle=3.14159 EndAngle=4.71239
    g20: GeomPoint [constr] X=-33.9761 Y=128.123 Z=0
  constraints (38):
    c: Coincident(g-3,g0)
    c: Horizontal(g0)
    c: Coincident(g0,g1)
    c: Vertical(g1)
    c: Horizontal(g2)
    c: Coincident(g2,g3)
    c: Vertical(g3)
    c: Horizontal(g4)
    c: Vertical(g5)
    c: Coincident(g5,g6)
    c: Horizontal(g6)
    c: Coincident(g6,g7)
    c: Vertical(g7)
    c: Horizontal(g8)
    c: Vertical(g9)
    c: Coincident(g9,g10)
    c: Coincident(g10,g0)
    c: Horizontal(g10)
    c: PointOnObject(g12,g3)
    c: PointOnObject(g12,g4)
    c: Tangent(g3,g11) = -1.5708
    c: Tangent(g4,g11) = -1.5708
    c: PointOnObject(g14,g1)
    c: PointOnObject(g14,g2)
    c: Tangent(g1,g13) = -1.5708
    c: Tangent(g2,g13) = -1.5708
    c: PointOnObject(g16,g8)
    c: PointOnObject(g16,g9)
    c: Tangent(g8,g15) = 1.5708
    c: Tangent(g9,g15) = 1.5708
    c: PointOnObject(g18,g7)
    c: PointOnObject(g18,g8)
    c: Tangent(g7,g17) = -1.5708
    c: Tangent(g8,g17) = -1.5708
    c: PointOnObject(g20,g4)
    c: PointOnObject(g20,g5)
    c: Tangent(g4,g19) = 1.5708
    c: Tangent(g5,g19) = 1.5708
FEATURE [PartDesign::Pad] Pad023
  BaseFeature = -> Mirrored005
  Direction = (0,-1,2e-16)
  Length = 17
  Length2 = 10
  Midplane = true
  Placement = pos=(0,-70.97,87.59) rot=(0.57735,-0.57735,0.57735;2.0944rad)
  Profile = -> Sketch040
  ReferenceAxis = -> Sketch040 [N_Axis]
  Refine = true
  Suppressed = false
  Type = 0
FEATURE [PartDesign::Plane] DatumPlane004
  AttachmentOffset = pos=(0,0,79) rot=(0,0,1;0rad)
  AttachmentSupport = -> [XY_Plane]
  Length = 97.5309
  MapMode = 5
  Placement = pos=(0,0,79) rot=(0,0,1;0rad)
  ResizeMode = 0
  Width = 260.825
FEATURE [Sketcher::SketchObject] Sketch041
  ArcFitTolerance = 1e-06
  AttachmentSupport = -> [DatumPlane004]
  ExternalGeometry = -> [Pad023]
  FullyConstrained = true
  MakeInternals = false
  MapMode = 5
  Placement = pos=(0,0,79) rot=(0,0,1;0rad)
  sketch-geometry (3):
    g0: Circle CenterX=21.13 CenterY=9 CenterZ=0 NormalX=0 NormalY=0 NormalZ=1 AngleXU=0 Radius=2
    g1: LineSegment [constr] StartX=23.73 StartY=9 StartZ=0 EndX=21.13 EndY=9 EndZ=0
    g2: GeomPoint X=21.13 Y=9 Z=0
  constraints (7):
    c: Diameter(g0) = 4
    c: Coincident(g1,g0)
    c: Horizontal(g1)
    c: Coincident(g1,g-6)
    c: DistanceX(g0,g1) = 2.6
    c: Distance(g0,g-1) = 9
    c: Coincident(g2,g0)
FEATURE [PartDesign::Plane] DatumPlane005
  AttachmentOffset = pos=(0,0,12) rot=(0,0,1;0rad)
  AttachmentSupport = -> [YZ_Plane]
  Length = 273.301
  MapMode = 5
  Placement = pos=(12,0,0) rot=(0.57735,0.57735,0.57735;2.0944rad)
  ResizeMode = 0
  Width = 195.457
FEATURE [Sketcher::SketchObject] Sketch042
  ArcFitTolerance = 1e-06
  AttachmentSupport = -> [DatumPlane005]
  ExternalGeometry = -> [Sketch041]
  FullyConstrained = true
  MakeInternals = false
  MapMode = 5
  Placement = pos=(12,0,0) rot=(0.57735,0.57735,0.57735;2.0944rad)
  sketch-geometry (4):
    g0: Circle CenterX=9 CenterY=50 CenterZ=0 NormalX=0 NormalY=0 NormalZ=1 AngleXU=0 Radius=2
    g1: GeomPoint X=9 Y=50 Z=0
    g2: LineSegment [constr] StartX=9 StartY=50 StartZ=0 EndX=9 EndY=79 EndZ=0
    g3: GeomPoint X=9 Y=50 Z=0
  constraints (7):
    c: Diameter(g0) = 4
    c: Coincident(g2,g-3)
    c: Vertical(g2)
    c: Coincident(g0,g1)
    c: Coincident(g0,g2)
    c: DistanceY(g-1,g0) = 50
    c: Coincident(g3,g0)
FEATURE [PartDesign::Plane] DatumPlane006
  AttachmentSupport = -> [Sketch042,XZ_Plane]
  Length = 178.251
  MapMode = 6
  Placement = pos=(12,9,50) rot=(0.57735,-0.57735,0.57735;2.0944rad)
  ResizeMode = 0
  Width = 92.8021
FEATURE [Sketcher::SketchObject] Sketch043
  ArcFitTolerance = 1e-06
  AttachmentSupport = -> [DatumPlane006]
  ExternalGeometry = -> [Sketch041]
  FullyConstrained = false
  MakeInternals = false
  MapMode = 5
  Placement = pos=(12,9,50) rot=(0.57735,-0.57735,0.57735;2.0944rad)
  sketch-geometry (4):
    g0: LineSegment StartX=29 StartY=-9.13 StartZ=0 EndX=8.42265 EndY=-9.13 EndZ=0
    g1: LineSegment StartX=0 StartY=-0.707348 StartZ=0 EndX=0 EndY=0 EndZ=0
    g2: ArcOfCircle CenterX=8.42265 CenterY=-0.707348 CenterZ=0 NormalX=0 NormalY=0 NormalZ=1 AngleXU=0 Radius=8.42265 StartAngle=3.14159 EndAngle=4.71239
    g3: GeomPoint [constr] X=0 Y=-9.13 Z=0
  constraints (8):
    c: Coincident(g0,g-3)
    c: PointOnObject(g3,g-2)
    c: Horizontal(g0)
    c: Coincident(g1,g-1)
    c: PointOnObject(g3,g0)
    c: PointOnObject(g3,g1)
    c: Tangent(g0,g2) = 1.5708
    c: Tangent(g1,g2) = 1.5708
FEATURE [PartDesign::AdditivePipe] AdditivePipe
  AuxilleryCurvelinear = true
  AuxillerySpineTangent = false
  BaseFeature = -> Pad023
  Binormal = (0,0,0)
  Mode = 0
  Placement = pos=(0,-70.97,87.59) rot=(0.57735,-0.57735,0.57735;2.0944rad)
  Profile = -> Sketch041
  Refine = true
  Sections = -> [Sketch042]
  Spine = -> Sketch043
  SpineTangent = false
  Suppressed = false
  Transformation = 1
  Transition = 0
FEATURE [PartDesign::Mirrored] Mirrored006
  MirrorPlane = -> Sketch041 [V_Axis]
  Placement = pos=(0,-70.97,87.59) rot=(0.57735,-0.57735,0.57735;2.0944rad)
  Refine = true
  Suppressed = false
  TransformMode = 0
FEATURE [PartDesign::Mirrored] Mirrored007
  MirrorPlane = -> XZ_Plane
  Placement = pos=(0,-70.97,87.59) rot=(0.57735,-0.57735,0.57735;2.0944rad)
  Refine = true
  Suppressed = false
  TransformMode = 0
FEATURE [PartDesign::MultiTransform] MultiTransform
  BaseFeature = -> AdditivePipe
  Originals = -> [AdditivePipe]
  Placement = pos=(0,-70.97,87.59) rot=(0.57735,-0.57735,0.57735;2.0944rad)
  Refine = true
  Suppressed = false
  TransformMode = 0
  Transformations = -> [Mirrored006,Mirrored007]
FEATURE [Sketcher::SketchObject] Sketch044
  ArcFitTolerance = 1e-06
  AttachmentSupport = -> [XZ_Plane]
  ExternalGeometry = -> [MultiTransform]
  FullyConstrained = true
  MakeInternals = false
  MapMode = 5
  Placement = pos=(0,0,0) rot=(1,0,0;1.5708rad)
  sketch-geometry (2):
    g0: Circle CenterX=-13.7073 CenterY=55 CenterZ=0 NormalX=0 NormalY=0 NormalZ=1 AngleXU=0 Radius=3
    g1: Circle CenterX=13.7073 CenterY=55 CenterZ=0 NormalX=0 NormalY=0 NormalZ=1 AngleXU=0 Radius=3
  constraints (6):
    c: Diameter(g0) = 6
    c: DistanceY(g-3,g0) = 3
    c: DistanceX(g0,g-3) = 1
    c: Diameter(g1) = 6
    c: DistanceY(g-4,g1) = 3
    c: DistanceX(g-4,g1) = 1
FEATURE [PartDesign::Pad] Pad024
  BaseFeature = -> MultiTransform
  Direction = (0,-1,2e-16)
  Length = 24
  Length2 = 10
  Midplane = true
  Placement = pos=(0,-70.97,87.59) rot=(0.57735,-0.57735,0.57735;2.0944rad)
  Profile = -> Sketch044
  ReferenceAxis = -> Sketch044 [N_Axis]
  Refine = true
  Suppressed = false
  Type = 0
FEATURE [Sketcher::SketchObject] Sketch045
  ArcFitTolerance = 1e-06
  AttachmentSupport = -> [YZ_Plane]
  FullyConstrained = false
  MakeInternals = false
  MapMode = 5
  Placement = pos=(0,0,0) rot=(0.57735,0.57735,0.57735;2.0944rad)
  sketch-geometry (4):
    g0: LineSegment StartX=-6.25515 StartY=112.828 StartZ=0 EndX=-6.25515 EndY=100.384 EndZ=0
    g1: LineSegment StartX=-6.25515 StartY=100.384 StartZ=0 EndX=7.71433 EndY=100.384 EndZ=0
    g2: LineSegment StartX=7.71433 StartY=100.384 StartZ=0 EndX=7.71433 EndY=112.828 EndZ=0
    g3: LineSegment StartX=7.71433 StartY=112.828 StartZ=0 EndX=-6.25515 EndY=112.828 EndZ=0
  constraints (8):
    c: Coincident(g0,g1)
    c: Coincident(g1,g2)
    c: Coincident(g2,g3)
    c: Coincident(g3,g0)
    c: Vertical(g0)
    c: Vertical(g2)
    c: Horizontal(g1)
    c: Horizontal(g3)
FEATURE [PartDesign::Pad] Pad025
  BaseFeature = -> Pad024
  Direction = (1,0,0)
  Length = 6
  Length2 = 10
  Midplane = true
  Placement = pos=(0,-70.97,87.59) rot=(0.57735,-0.57735,0.57735;2.0944rad)
  Profile = -> Sketch045
  ReferenceAxis = -> Sketch045 [N_Axis]
  Refine = true
  Suppressed = false
  Type = 0
FEATURE [Sketcher::SketchObject] Sketch046
  ArcFitTolerance = 1e-06
  AttachmentSupport = -> [YZ_Plane]
  FullyConstrained = false
  MakeInternals = false
  MapMode = 5
  Placement = pos=(0,0,0) rot=(0.57735,0.57735,0.57735;2.0944rad)
  sketch-geometry (15):
    g0: LineSegment StartX=-57.593 StartY=121.025 StartZ=0 EndX=-43.3744 EndY=121.025 EndZ=0
    g1: LineSegment StartX=-43.3744 StartY=121.025 StartZ=0 EndX=-24.2528 EndY=117.397 EndZ=0
    g2: LineSegment StartX=-24.2528 StartY=117.397 StartZ=0 EndX=21.443 EndY=117.397 EndZ=0
    g3: LineSegment StartX=21.443 StartY=117.397 StartZ=0 EndX=24.2867 EndY=119.26 EndZ=0
    g4: LineSegment StartX=24.2867 StartY=119.26 StartZ=0 EndX=35.5636 EndY=119.26 EndZ=0
    g5: LineSegment StartX=35.5636 StartY=119.26 StartZ=0 EndX=35.5636 EndY=121.515 EndZ=0
    g6: LineSegment StartX=35.5636 StartY=121.515 StartZ=0 EndX=41.929 EndY=121.515 EndZ=0
    g7: LineSegment StartX=41.929 StartY=121.515 StartZ=0 EndX=41.929 EndY=119.048 EndZ=0
    g8: LineSegment StartX=41.929 StartY=119.048 StartZ=0 EndX=44.3713 EndY=119.048 EndZ=0
    g9: LineSegment StartX=44.3713 StartY=119.048 StartZ=0 EndX=44.3713 EndY=120.886 EndZ=0
    g10: LineSegment StartX=44.3713 StartY=120.886 StartZ=0 EndX=45.9443 EndY=120.886 EndZ=0
    g11: LineSegment StartX=45.9443 StartY=120.886 StartZ=0 EndX=45.9443 EndY=119.29 EndZ=0
    g12: LineSegment StartX=-57.593 StartY=121.025 StartZ=0 EndX=-57.593 EndY=112.568 EndZ=0
    g13: LineSegment StartX=-57.593 StartY=112.568 StartZ=0 EndX=45.9443 EndY=112.568 EndZ=0
    g14: LineSegment StartX=45.9443 StartY=112.568 StartZ=0 EndX=45.9443 EndY=119.29 EndZ=0
  constraints (28):
    c: Horizontal(g0)
    c: Coincident(g0,g1)
    c: Coincident(g1,g2)
    c: Horizontal(g2)
    c: Coincident(g2,g3)
    c: Coincident(g3,g4)
    c: Horizontal(g4)
    c: Coincident(g4,g5)
    c: Vertical(g5)
    c: Coincident(g5,g6)
    c: Horizontal(g6)
    c: Coincident(g6,g7)
    c: Vertical(g7)
    c: Coincident(g7,g8)
    c: Horizontal(g8)
    c: Coincident(g8,g9)
    c: Vertical(g9)
    c: Coincident(g9,g10)
    c: Horizontal(g10)
    c: Coincident(g10,g11)
    c: Vertical(g11)
    c: Coincident(g12,g0)
    c: Vertical(g12)
    c: Coincident(g12,g13)
    c: Horizontal(g13)
    c: Coincident(g13,g14)
    c: Coincident(g14,g11)
    c: Vertical(g14)
FEATURE [PartDesign::Revolution] Revolution002
  Angle = 360
  Angle2 = 60
  Axis = (0,1,0)
  Base = (0,-57.593,112.568)
  BaseFeature = -> Pad025
  Placement = pos=(0,-70.97,87.59) rot=(0.57735,-0.57735,0.57735;2.0944rad)
  Profile = -> Sketch046
  ReferenceAxis = -> Sketch046 [Edge14]
  Refine = true
  Suppressed = false
  Type = 0
FEATURE [Sketcher::SketchObject] Sketch047
  ArcFitTolerance = 1e-06
  AttachmentSupport = -> [YZ_Plane]
  FullyConstrained = false
  MakeInternals = false
  MapMode = 5
  Placement = pos=(0,0,0) rot=(0.57735,0.57735,0.57735;2.0944rad)
  sketch-geometry (4):
    g0: LineSegment StartX=45.4214 StartY=121.509 StartZ=0 EndX=45.4214 EndY=103.642 EndZ=0
    g1: LineSegment StartX=45.4214 StartY=103.642 StartZ=0 EndX=76.8501 EndY=103.642 EndZ=0
    g2: LineSegment StartX=76.8501 StartY=103.642 StartZ=0 EndX=76.8501 EndY=121.509 EndZ=0
    g3: LineSegment StartX=76.8501 StartY=121.509 StartZ=0 EndX=45.4214 EndY=121.509 EndZ=0
  constraints (8):
    c: Coincident(g0,g1)
    c: Coincident(g1,g2)
    c: Coincident(g2,g3)
    c: Coincident(g3,g0)
    c: Vertical(g0)
    c: Vertical(g2)
    c: Horizontal(g1)
    c: Horizontal(g3)
FEATURE [PartDesign::Pad] Pad026
  BaseFeature = -> Revolution002
  Direction = (1,0,0)
  Length = 19
  Length2 = 10
  Midplane = true
  Placement = pos=(0,-70.97,87.59) rot=(0.57735,-0.57735,0.57735;2.0944rad)
  Profile = -> Sketch047
  ReferenceAxis = -> Sketch047 [N_Axis]
  Refine = true
  Suppressed = false
  Type = 0
FEATURE [PartDesign::Fillet] Fillet003
  Base = -> Pad026 [Edge2268,Edge2271,Edge2267,Edge2269]
  BaseFeature = -> Pad026
  Placement = pos=(0,-70.97,87.59) rot=(0.57735,-0.57735,0.57735;2.0944rad)
  Radius = 5
  Refine = true
  SupportTransform = false
  Suppressed = false
  UseAllEdges = false
FEATURE [Sketcher::SketchObject] Sketch048
  ArcFitTolerance = 1e-06
  AttachmentSupport = -> [YZ_Plane]
  FullyConstrained = false
  MakeInternals = false
  MapMode = 5
  Placement = pos=(0,0,0) rot=(0.57735,0.57735,0.57735;2.0944rad)
  sketch-geometry (4):
    g0: LineSegment StartX=-13.0809 StartY=118.504 StartZ=0 EndX=-13.0809 EndY=106.504 EndZ=0
    g1: LineSegment StartX=-13.0809 StartY=106.504 StartZ=0 EndX=-1.08088 EndY=106.504 EndZ=0
    g2: LineSegment StartX=-1.08088 StartY=106.504 StartZ=0 EndX=-1.08088 EndY=118.504 EndZ=0
    g3: LineSegment StartX=-1.08088 StartY=118.504 StartZ=0 EndX=-13.0809 EndY=118.504 EndZ=0
  constraints (10):
    c: Coincident(g0,g1)
    c: Coincident(g1,g2)
    c: Coincident(g2,g3)
    c: Coincident(g3,g0)
    c: Vertical(g0)
    c: Vertical(g2)
    c: Horizontal(g1)
    c: Horizontal(g3)
    c: DistanceX(g3,g3) = 12
    c: DistanceY(g2,g2) = 12
FEATURE [PartDesign::Pad] Pad027
  BaseFeature = -> Fillet003
  Direction = (1,0,0)
  Length = 12
  Length2 = 10
  Midplane = true
  Placement = pos=(0,-70.97,87.59) rot=(0.57735,-0.57735,0.57735;2.0944rad)
  Profile = -> Sketch048
  ReferenceAxis = -> Sketch048 [N_Axis]
  Refine = true
  Suppressed = false
  Type = 0
FEATURE [PartDesign::Chamfer] Chamfer001
  Angle = 45
  Base = -> Pad027 [Face26,Face25,Face24]
  BaseFeature = -> Pad027
  ChamferType = 0
  FlipDirection = false
  Placement = pos=(0,-70.97,87.59) rot=(0.57735,-0.57735,0.57735;2.0944rad)
  Refine = true
  Size = 1
  Size2 = 1
  SupportTransform = false
  Suppressed = false
  UseAllEdges = false
FEATURE [Sketcher::SketchObject] Sketch049
  ArcFitTolerance = 1e-06
  AttachmentSupport = -> [YZ_Plane]
  ExternalGeometry = -> [Chamfer001]
  FullyConstrained = true
  MakeInternals = false
  MapMode = 5
  Placement = pos=(0,0,0) rot=(0.57735,0.57735,0.57735;2.0944rad)
  sketch-geometry (2):
    g0: LineSegment [constr] StartX=-12.0809 StartY=112.504 StartZ=0 EndX=-2.08088 EndY=112.504 EndZ=0
    g1: Circle CenterX=-7.08088 CenterY=112.504 CenterZ=0 NormalX=0 NormalY=0 NormalZ=1 AngleXU=0 Radius=2.5
  constraints (4):
    c: Symmetric(g-3,g-3,g0)
    c: Symmetric(g-4,g-4,g0)
    c: Symmetric(g0,g0,g1)
    c: Diameter(g1) = 5
FEATURE [PartDesign::Pad] Pad028
  BaseFeature = -> Chamfer001
  Direction = (1,0,0)
  Length = 18
  Length2 = 10
  Midplane = true
  Placement = pos=(0,-70.97,87.59) rot=(0.57735,-0.57735,0.57735;2.0944rad)
  Profile = -> Sketch049
  ReferenceAxis = -> Sketch049 [N_Axis]
  Refine = true
  Suppressed = false
  Type = 0
FEATURE [Sketcher::SketchObject] Sketch050
  ArcFitTolerance = 1e-06
  AttachmentSupport = -> [Pad028]
  ExternalGeometry = -> [Pad028]
  FullyConstrained = true
  MakeInternals = false
  MapMode = 5
  Placement = pos=(0,-70.97,118.504) rot=(0,0,1;3.14159rad)
  sketch-geometry (2):
    g0: LineSegment [constr] StartX=5.15e-14 StartY=-58.8891 StartZ=0 EndX=6.04e-14 EndY=-68.8891 EndZ=0
    g1: Circle CenterX=5.6e-14 CenterY=-63.8891 CenterZ=0 NormalX=0 NormalY=0 NormalZ=1 AngleXU=0 Radius=2.5
  constraints (4):
    c: Symmetric(g-3,g-3,g0)
    c: Symmetric(g-4,g-4,g0)
    c: Symmetric(g0,g0,g1)
    c: Diameter(g1) = 5
FEATURE [PartDesign::Pad] Pad029
  BaseFeature = -> Pad028
  Direction = (0,0,1)
  Length = 3
  Length2 = 10
  Placement = pos=(0,-70.97,87.59) rot=(0.57735,-0.57735,0.57735;2.0944rad)
  Profile = -> Sketch050
  ReferenceAxis = -> Sketch050 [N_Axis]
  Refine = true
  Suppressed = false
  Type = 0
FEATURE [PartDesign::Plane] DatumPlane007
  AttachmentOffset = pos=(0,0,75) rot=(0,0,1;0rad)
  AttachmentSupport = -> [XY_Plane]
  Length = 97.5309
  MapMode = 5
  Placement = pos=(0,0,75) rot=(0,0,1;0rad)
  ResizeMode = 0
  Width = 260.825
FEATURE [Sketcher::SketchObject] Sketch051
  ArcFitTolerance = 1e-06
  AttachmentSupport = -> [DatumPlane007]
  ExternalGeometry = -> [Pad029]
  FullyConstrained = true
  MakeInternals = false
  MapMode = 5
  Placement = pos=(0,0,75) rot=(0,0,1;0rad)
  sketch-geometry (6):
    g0: LineSegment StartX=-3.36603 StartY=-21.4223 StartZ=0 EndX=-3.36603 EndY=0.297535 EndZ=0
    g1: LineSegment StartX=-3.36603 StartY=0.297535 StartZ=0 EndX=3.36603 EndY=0.297535 EndZ=0
    g2: LineSegment StartX=3.36603 StartY=0.297535 StartZ=0 EndX=3.36603 EndY=-21.4223 EndZ=0
    g3: LineSegment StartX=3.36603 StartY=-21.4223 StartZ=0 EndX=-3.36603 EndY=-21.4223 EndZ=0
    g4: LineSegment [constr] StartX=-2.102e-13 StartY=0.297535 StartZ=0 EndX=-2.102e-13 EndY=-21.4223 EndZ=0
    g5: GeomPoint X=-2.102e-13 Y=-10.5624 Z=0
  constraints (15):
    c: Coincident(g0,g1)
    c: Coincident(g1,g2)
    c: Coincident(g2,g3)
    c: Coincident(g3,g0)
    c: Vertical(g0)
    c: Vertical(g2)
    c: Horizontal(g1)
    c: Horizontal(g3)
    c: Distance(g-4,g0) = 1
    c: Distance(g-5,g2) = 1
    c: Distance(g-6,g1) = 1
    c: Distance(g-3,g3) = 1
    c: Symmetric(g1,g1,g4)
    c: Symmetric(g3,g3,g4)
    c: Symmetric(g4,g4,g5)
FEATURE [PartDesign::Plane] DatumPlane008
  AttachmentOffset = pos=(0,0,66) rot=(0,0,1;0rad)
  AttachmentSupport = -> [XY_Plane]
  Length = 97.5309
  MapMode = 5
  Placement = pos=(0,0,66) rot=(0,0,1;0rad)
  ResizeMode = 0
  Width = 260.825
FEATURE [Sketcher::SketchObject] Sketch052
  ArcFitTolerance = 1e-06
  AttachmentSupport = -> [DatumPlane008]
  FullyConstrained = false
  MakeInternals = false
  MapMode = 5
  Placement = pos=(0,0,66) rot=(0,0,1;0rad)
  sketch-geometry (6):
    g0: LineSegment StartX=-3.5133 StartY=0.500097 StartZ=0 EndX=-3.5133 EndY=-21.5599 EndZ=0
    g1: LineSegment StartX=-3.5133 StartY=-21.5599 StartZ=0 EndX=3.2167 EndY=-21.5599 EndZ=0
    g2: LineSegment StartX=3.2167 StartY=-21.5599 StartZ=0 EndX=3.2167 EndY=0.500097 EndZ=0
    g3: LineSegment StartX=3.2167 StartY=0.500097 StartZ=0 EndX=-3.5133 EndY=0.500097 EndZ=0
    g4: LineSegment [constr] StartX=-0.148302 StartY=-21.5599 StartZ=0 EndX=-0.148302 EndY=0.500097 EndZ=0
    g5: GeomPoint X=-0.148302 Y=-10.5299 Z=0
  constraints (13):
    c: Coincident(g0,g1)
    c: Coincident(g1,g2)
    c: Coincident(g2,g3)
    c: Coincident(g3,g0)
    c: Vertical(g0)
    c: Vertical(g2)
    c: Horizontal(g1)
    c: Horizontal(g3)
    c: DistanceY(g0,g0) = 22.06
    c: DistanceX(g1,g1) = 6.73
    c: Symmetric(g1,g1,g4)
    c: Symmetric(g3,g3,g4)
    c: Symmetric(g4,g4,g5)
FEATURE [PartDesign::Plane] DatumPlane009
  AttachmentOffset = pos=(0,0,-7) rot=(0,0,1;0rad)
  AttachmentSupport = -> [YZ_Plane]
  Length = 273.301
  MapMode = 5
  Placement = pos=(-7,0,0) rot=(0.57735,0.57735,0.57735;2.0944rad)
  ResizeMode = 0
  Width = 195.457
FEATURE [Sketcher::SketchObject] Sketch053
  ArcFitTolerance = 1e-06
  AttachmentSupport = -> [DatumPlane009]
  FullyConstrained = false
  MakeInternals = false
  MapMode = 5
  Placement = pos=(-7,0,0) rot=(0.57735,0.57735,0.57735;2.0944rad)
  sketch-geometry (6):
    g0: LineSegment StartX=0.309038 StartY=63.6282 StartZ=0 EndX=-21.751 EndY=63.6282 EndZ=0
    g1: LineSegment StartX=-21.751 StartY=63.6282 StartZ=0 EndX=-21.751 EndY=56.8982 EndZ=0
    g2: LineSegment StartX=-21.751 StartY=56.8982 StartZ=0 EndX=0.309038 EndY=56.8982 EndZ=0
    g3: LineSegment StartX=0.309038 StartY=56.8982 StartZ=0 EndX=0.309038 EndY=63.6282 EndZ=0
    g4: LineSegment [constr] StartX=-21.751 StartY=60.2632 StartZ=0 EndX=0.309038 EndY=60.2632 EndZ=0
    g5: GeomPoint X=-10.721 Y=60.2632 Z=0
  constraints (13):
    c: Coincident(g0,g1)
    c: Coincident(g1,g2)
    c: Coincident(g2,g3)
    c: Coincident(g3,g0)
    c: DistanceY(g1,g1) = 6.73
    c: DistanceX(g0,g0) = 22.06
    c: Horizontal(g0)
    c: Horizontal(g2)
    c: Vertical(g1)
    c: Vertical(g3)
    c: Symmetric(g1,g1,g4)
    c: Symmetric(g3,g3,g4)
    c: Symmetric(g4,g4,g5)
FEATURE [Sketcher::SketchObject] Sketch054
  ArcFitTolerance = 1e-06
  AttachmentSupport = -> [Pad029]
  FullyConstrained = false
  MakeInternals = false
  MapMode = 5
  Placement = pos=(-23.73,-70.97,87.59) rot=(0.707107,0,0.707107;3.14159rad)
  sketch-geometry (6):
    g0: LineSegment StartX=-17.07 StartY=-82.3783 StartZ=0 EndX=-17.07 EndY=-60.3183 EndZ=0
    g1: LineSegment StartX=-17.07 StartY=-60.3183 StartZ=0 EndX=-23.8 EndY=-60.3183 EndZ=0
    g2: LineSegment StartX=-23.8 StartY=-60.3183 StartZ=0 EndX=-23.8 EndY=-82.3783 EndZ=0
    g3: LineSegment StartX=-23.8 StartY=-82.3783 StartZ=0 EndX=-17.07 EndY=-82.3783 EndZ=0
    g4: LineSegment [constr] StartX=-20.435 StartY=-60.3183 StartZ=0 EndX=-20.435 EndY=-82.3783 EndZ=0
    g5: GeomPoint X=-20.435 Y=-71.3483 Z=0
  constraints (13):
    c: Coincident(g0,g1)
    c: Coincident(g1,g2)
    c: Coincident(g2,g3)
    c: Coincident(g3,g0)
    c: DistanceY(g2,g2) = 22.06
    c: DistanceX(g1,g1) = 6.73
    c: Horizontal(g1)
    c: Vertical(g2)
    c: Vertical(g0)
    c: Horizontal(g3)
    c: Symmetric(g1,g1,g4)
    c: Symmetric(g3,g3,g4)
    c: Symmetric(g4,g4,g5)
FEATURE [Sketcher::SketchObject] Sketch055
  ArcFitTolerance = 1e-06
  AttachmentSupport = -> [Pad029]
  ExternalGeometry = -> [Pad029]
  FullyConstrained = true
  MakeInternals = false
  MapMode = 5
  Placement = pos=(0,-57.593,87.59) rot=(0.57735,-0.57735,0.57735;2.0944rad)
  sketch-geometry (1):
    g0: Circle CenterX=24.9777 CenterY=4.85e-14 CenterZ=0 NormalX=0 NormalY=0 NormalZ=1 AngleXU=0 Radius=7.45734
  constraints (2):
    c: Coincident(g0,g-3)
    c: Distance(g0,g-3) = 1
FEATURE [PartDesign::Pocket] Pocket011
  BaseFeature = -> Pad029
  Direction = (-2.2e-15,1,0)
  Length = 5
  Length2 = 5
  Placement = pos=(0,-70.97,87.59) rot=(0.57735,-0.57735,0.57735;2.0944rad)
  Profile = -> Sketch055
  ReferenceAxis = -> Sketch055 [N_Axis]
  Refine = true
  Suppressed = false
  Type = 0
FEATURE [Part::Part2DObjectPython] Wire  # Draft 2D object (typed FeaturePython)
  Area = 0
  ChamferSize = 0
  Closed = false
  End = (-23.73,0.378266,67.155)
  FilletRadius = 5
  Length = 38.0962
  MakeFace = true
  Placement = pos=(-2.102e-13,-10.5624,75) rot=(0,0,1;0rad)
  Points = (4) [(0,0,0),(-0.148302,0.0324585,-9),(-7,-0.158601,-14.7368),(-23.73,10.9406,-7.84497)]
  Start = (-2.102e-13,-10.5624,75)
  Subdivisions = 0
FEATURE [Sketcher::SketchObject] Sketch056
  ArcFitTolerance = 1e-06
  AttachmentSupport = -> [Pocket011]
  ExternalGeometry = -> [Pocket011]
  FullyConstrained = true
  MakeInternals = false
  MapMode = 5
  Placement = pos=(-28.73,-70.97,87.59) rot=(0.707107,0,-0.707107;3.14159rad)
  sketch-geometry (1):
    g0: Circle CenterX=7.59 CenterY=-70.97 CenterZ=0 NormalX=0 NormalY=0 NormalZ=1 AngleXU=0 Radius=2.45
  constraints (2):
    c: Diameter(g0) = 4.9
    c: Coincident(g0,g-3)
FEATURE [PartDesign::Pocket] Pocket012
  BaseFeature = -> Pocket011
  Direction = (1,0,2e-16)
  Length = 8
  Length2 = 5
  Placement = pos=(0,-70.97,87.59) rot=(0.57735,-0.57735,0.57735;2.0944rad)
  Profile = -> Sketch056
  ReferenceAxis = -> Sketch056 [N_Axis]
  Refine = true
  Suppressed = false
  Type = 0
FEATURE [Sketcher::SketchObject] Sketch057
  ArcFitTolerance = 1e-06
  AttachmentSupport = -> [Pocket012]
  ExternalGeometry = -> [Pocket012]
  FullyConstrained = false
  MakeInternals = false
  MapMode = 5
  Placement = pos=(-28.73,-70.97,87.59) rot=(0.707107,0,-0.707107;3.14159rad)
  sketch-geometry (16):
    g0: ArcOfCircle CenterX=9.7 CenterY=-70.9697 CenterZ=0 NormalX=0 NormalY=0 NormalZ=1 AngleXU=0 Radius=6.01 StartAngle=3.14164 EndAngle=3.55318
    g1: LineSegment StartX=4.19192 StartY=-73.3741 StartZ=0 EndX=4.30394 EndY=-73.6307 EndZ=0
    g2: LineSegment StartX=4.30394 StartY=-73.6307 StartZ=0 EndX=4.99 EndY=-84.97 EndZ=0
    g3: ArcOfCircle CenterX=7.59 CenterY=-84.6469 CenterZ=0 NormalX=0 NormalY=0 NormalZ=1 AngleXU=0 Radius=2.62 StartAngle=3.26523 EndAngle=4.71239
    g4: ArcOfCircle CenterX=5.48 CenterY=-70.9702 CenterZ=0 NormalX=0 NormalY=0 NormalZ=1 AngleXU=0 Radius=6.01 StartAngle=5.87243 EndAngle=6.28322
    g5: LineSegment StartX=10.9901 StartY=-73.37 StartZ=0 EndX=10.8765 EndY=-73.6308 EndZ=0
    g6: LineSegment StartX=10.8765 StartY=-73.6308 StartZ=0 EndX=10.19 EndY=-84.97 EndZ=0
    g7: ArcOfCircle CenterX=7.59 CenterY=-84.6469 CenterZ=0 NormalX=0 NormalY=0 NormalZ=1 AngleXU=0 Radius=2.62 StartAngle=4.71239 EndAngle=6.15955
    g8: ArcOfCircle CenterX=9.7 CenterY=-70.9699 CenterZ=0 NormalX=0 NormalY=0 NormalZ=1 AngleXU=0 Radius=6.01 StartAngle=2.73017 EndAngle=3.14161
    g9: LineSegment StartX=4.19151 StartY=-68.5664 StartZ=0 EndX=4.30349 EndY=-68.3098 EndZ=0
    g10: LineSegment StartX=4.30349 StartY=-68.3098 StartZ=0 EndX=4.98964 EndY=-56.9698 EndZ=0
    g11: ArcOfCircle CenterX=7.59 CenterY=-57.29 CenterZ=0 NormalX=0 NormalY=0 NormalZ=1 AngleXU=0 Radius=2.62 StartAngle=1.5708 EndAngle=3.01907
    g12: ArcOfCircle CenterX=5.48 CenterY=-70.9699 CenterZ=0 NormalX=0 NormalY=0 NormalZ=1 AngleXU=0 Radius=6.01 StartAngle=6.28317 EndAngle=6.6946
    g13: LineSegment StartX=10.9885 StartY=-68.5664 StartZ=0 EndX=10.8765 EndY=-68.3098 EndZ=0
    g14: LineSegment StartX=10.8765 StartY=-68.3098 StartZ=0 EndX=10.1904 EndY=-56.9698 EndZ=0
    g15: ArcOfCircle CenterX=7.59 CenterY=-57.29 CenterZ=0 NormalX=0 NormalY=0 NormalZ=1 AngleXU=0 Radius=2.62 StartAngle=0.122522 EndAngle=1.5708
  constraints (50):
    c: Tangent(g0,g1) = -1.5708
    c: Coincident(g1,g2)
    c: Coincident(g3,g2)
    c: Tangent(g4,g5) = 1.5708
    c: Coincident(g5,g6)
    c: Coincident(g7,g6)
    c: Tangent(g8,g9) = 1.5708
    c: Coincident(g9,g10)
    c: Coincident(g11,g10)
    c: Tangent(g12,g13) = -1.5708
    c: Coincident(g13,g14)
    c: Coincident(g15,g14)
    c: Coincident(g15,g11)
    c: Coincident(g11,g15)
    c: Coincident(g3,g7)
    c: Coincident(g0,g8)
    c: Coincident(g4,g12)
    c: DistanceX(g-1,g11) = 7.59
    c: DistanceY(g11,g-1) = 57.29
    c: DistanceX(g-1,g11) = 7.59
    c: DistanceY(g11,g11) = 2.62
    c: Angle(g15) = 1.44827
    c: Angle(g11) = 1.44827
    c: DistanceY(g10,g10) = 11.34
    c: Distance(g9,g9) = 0.28
    c: Radius(g8) = 6.01
    c: Radius(g0) = 6.01
    c: DistanceY(g14,g14) = 11.34
    c: Distance(g13,g13) = 0.28
    c: Angle(g13,g14) = 2.79061
    c: DistanceX(g-1,g3) = 7.59
    c: Distance(g1,g1) = 0.28
    c: Radius(g4) = 6.01
    c: Radius(g12) = 6.01
    c: DistanceX(g4,g-3) = 2.11
    c: DistanceX(g-3,g0) = 2.11
    c: Distance(g6,g6) = 11.36
    c: Distance(g2,g2) = 11.36
    c: Radius(g3) = 2.62
    c: Radius(g7) = 2.62
    c: DistanceX(g-1,g2) = 4.99
    c: DistanceX(g-1,g6) = 10.19
    c: DistanceX(g-1,g3) = 7.59
    c: DistanceY(g6,g-1) = 84.97
    c: DistanceY(g2,g-1) = 84.97
    c: Angle(g1,g2) = 2.79043
    c: Angle(g10,g9) = 2.79061
    c: Angle(g6,g5) = 2.79131
    c: DistanceY(g0,g-1) = 70.97
    c: DistanceY(g4,g-1) = 70.97
FEATURE [Sketcher::SketchObject] Sketch058
  ArcFitTolerance = 1e-06
  AttachmentSupport = -> [Pocket012]
  ExternalGeometry = -> [Pocket012]
  FullyConstrained = true
  MakeInternals = false
  MapMode = 5
  Placement = pos=(0,-70.97,128.123) rot=(0,0,1;3.14159rad)
  sketch-geometry (2):
    g0: Circle CenterX=31.1344 CenterY=-75.47 CenterZ=0 NormalX=0 NormalY=0 NormalZ=1 AngleXU=0 Radius=1.5
    g1: Circle CenterX=31.1344 CenterY=-66.47 CenterZ=0 NormalX=0 NormalY=0 NormalZ=1 AngleXU=0 Radius=1.5
  constraints (6):
    c: Diameter(g1) = 3
    c: Equal(g0,g1)
    c: Vertical(g0,g1)
    c: Distance(g1,g-3) = 4
    c: Distance(g0,g-4) = 4
    c: DistanceX(g-3,g1) = 5
FEATURE [PartDesign::Pocket] Pocket014
  BaseFeature = -> Pocket012
  Direction = (0,0,-1)
  Length = 5
  Length2 = 5
  Placement = pos=(0,-70.97,87.59) rot=(0.57735,-0.57735,0.57735;2.0944rad)
  Profile = -> Sketch058
  ReferenceAxis = -> Sketch058 [N_Axis]
  Refine = true
  Suppressed = false
  Type = 0
FEATURE [PartDesign::Body] Body  label="TurretGun"
  AllowCompound = false
  Group = -> [Sketch,DatumPlane,Sketch001,Pad,Sketch002,Sketch003,Pad001,Mirrored,Sketch004,Pad002,Sketch005,Pocket,Mirrored001,Fillet,Fillet001,Fillet002,Pad003,Sketch006,Pad004,Sketch008,Pad006,Sketch009,Pad007,Sketch010,Pad008,Pocket001,Sketch011,Pad009,Pocket002,Mirrored002,Sketch012,Pad010,Sketch013,Pad011,Sketch014,Pad012,Sketch015,Pad013,Sketch016,Pocket003,Sketch017,Pocket004,LinearPattern,Sketch018,+90 more]
  Origin = -> Origin
  Tip = -> Pocket014
